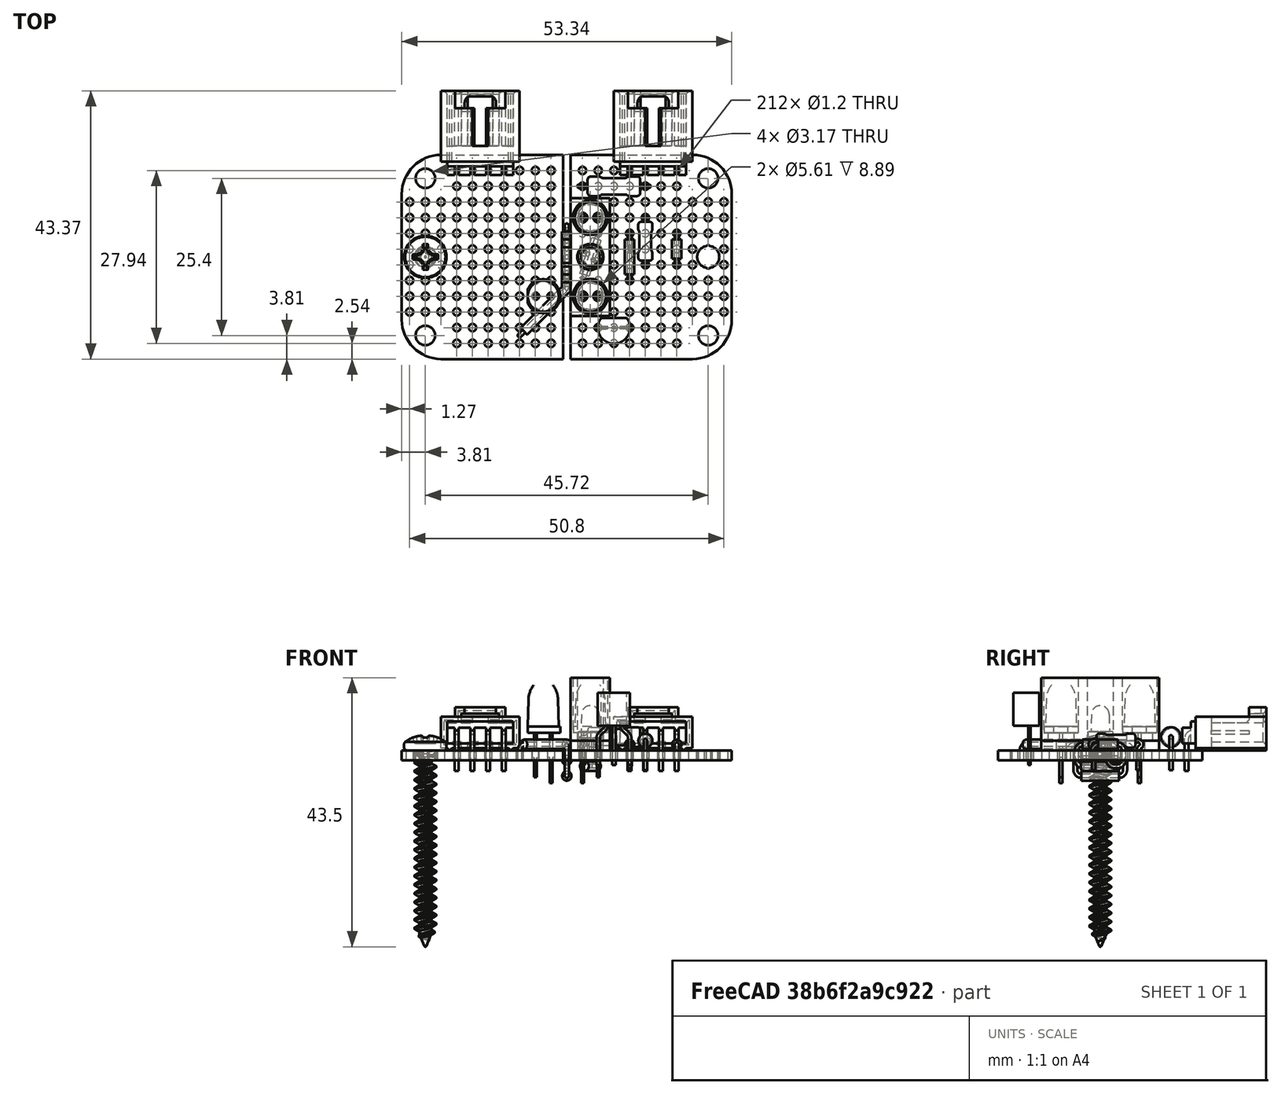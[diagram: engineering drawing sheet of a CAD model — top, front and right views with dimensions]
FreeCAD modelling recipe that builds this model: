
FCSTD DOCUMENT  (FreeCAD 0.21R33771 (Git))
Label: Sensor
License: All rights reserved
LicenseURL: http://en.wikipedia.org/wiki/All_rights_reserved
objects: Sketcher::SketchObject×51, PartDesign::Body×23, TechDraw::DrawViewDimension×21, PartDesign::Pad×16, Part::FeaturePython×14, PartDesign::AdditivePipe×10, PartDesign::LinearPattern×8, PartDesign::Pocket×8, App::Part×7, PartDesign::Revolution×4, PartDesign::MultiTransform×4, TechDraw::DrawProjGroupItem×3, Part::Feature×2, PartDesign::Mirrored×2, TechDraw::DrawSVGTemplate×2, TechDraw::DrawProjGroup×2, TechDraw::DrawPage×2, TechDraw::DrawViewSection×1, PartDesign::SubShapeBinder×1
note: 220 computed .brp shape members not serialized (recipe doc carries the construction recipe); baked Part::Feature solids carry a one-line shape summary decoded from their .brp

FEATURE [Part::Feature] Part__Feature  label="705530003"
  Placement = pos=(-13.97,-21.1455,4.5085) rot=(1,0,0;1.5708rad)
  shape: bbox 12.7 x 13.59 x 10.29 mm, 137 faces (baked)
FEATURE [Part::FeaturePython] Clone  label="705530003-001"  # Draft clone (typed FeaturePython)
  AttacherType = Attacher::AttachEngine3D
  Fuse = false
  Objects = -> [Part__Feature]
  Placement = pos=(-13.97,21.1455,4.5085) rot=(0,0.707107,0.707107;3.14159rad)
  Scale = (1,1,1)
FEATURE [Sketcher::SketchObject] Sketch
  FullyConstrained = true
  MapMode = 5
  Support = -> [XY_Plane]
  sketch-geometry (3):
    g0: ArcOfCircle CenterX=0 CenterY=0 CenterZ=0 NormalX=0 NormalY=0 NormalZ=1 AngleXU=0 Radius=2 StartAngle=5.43512 EndAngle=10.2728
    g1: LineSegment StartX=-1.32288 StartY=-1.5 StartZ=0 EndX=1.32288 EndY=-1.5 EndZ=0
    g2: Circle CenterX=0 CenterY=0 CenterZ=0 NormalX=0 NormalY=0 NormalZ=1 AngleXU=0 Radius=1.5
  constraints (8):
    c: Coincident(g0,g-1)
    c: Coincident(g1,g0)
    c: Coincident(g1,g0)
    c: Horizontal(g1)
    c: Diameter(g0) = 4
    c: Coincident(g2,g0)
    c: Diameter(g2) = 3
    c: Tangent(g1,g2)
FEATURE [PartDesign::Pad] Pad
  Direction = (0,0,1)
  Length = 1
  Length2 = 10
  Profile = -> Sketch
  ReferenceAxis = -> Sketch [N_Axis]
  Type = 0
FEATURE [Sketcher::SketchObject] Sketch001
  ExternalGeometry = -> [Sketch]
  FullyConstrained = true
  MapMode = 5
  Placement = pos=(0,0,0) rot=(0.57735,0.57735,0.57735;2.0944rad)
  Support = -> [YZ_Plane]
  sketch-geometry (4):
    g0: LineSegment StartX=0 StartY=5.2 StartZ=0 EndX=0 EndY=1 EndZ=0
    g1: LineSegment StartX=0 StartY=1 StartZ=0 EndX=-1.5 EndY=1 EndZ=0
    g2: LineSegment StartX=-1.5 StartY=1 StartZ=0 EndX=-1.42641 EndY=3.81046 EndZ=0
    g3: ArcOfCircle CenterX=0 CenterY=3.77311 CenterZ=0 NormalX=0 NormalY=0 NormalZ=1 AngleXU=0 Radius=1.42689 StartAngle=1.5708 EndAngle=3.11541
  constraints (12):
    c: PointOnObject(g0,g-2)
    c: DistanceY(g-1,g0) = 5.2
    c: Vertical(g0)
    c: Coincident(g0,g1)
    c: Horizontal(g1)
    c: Coincident(g1,g2)
    c: Tangent(g2,g3) = 1.5708
    c: Angle(g2) = 1.54462
    c: Vertical(g1,g-3)
    c: DistanceY(g-1,g1) = 1
    c: Coincident(g3,g0)
    c: PointOnObject(g3,g-2)
FEATURE [PartDesign::Revolution] Revolution
  Angle = 360
  Axis = (-2e-16,3e-16,1)
  Base = (0,0,0)
  BaseFeature = -> Pad
  Profile = -> Sketch001
  ReferenceAxis = -> Sketch001 [V_Axis]
FEATURE [Sketcher::SketchObject] Sketch002
  FullyConstrained = true
  MapMode = 5
  Placement = pos=(0,0,0) rot=(0.57735,0.57735,0.57735;2.0944rad)
  Support = -> [YZ_Plane]
  sketch-geometry (33):
    g0: LineSegment StartX=-0.325 StartY=0 StartZ=0 EndX=-1.52 EndY=0 EndZ=0
    g1: LineSegment StartX=0.325 StartY=0 StartZ=0 EndX=1.52 EndY=0 EndZ=0
    g2: LineSegment StartX=-2.04605 StartY=-1.71307 StartZ=0 EndX=-2.04605 EndY=-3.175 EndZ=0
    g3: LineSegment StartX=-2.04605 StartY=-3.175 StartZ=0 EndX=-1.54605 EndY=-3.175 EndZ=0
    g4: LineSegment StartX=-1.54605 StartY=-3.175 StartZ=0 EndX=-1.54605 EndY=-1.71307 EndZ=0
    g5: LineSegment StartX=2.04605 StartY=-1.71307 StartZ=0 EndX=2.04605 EndY=-3.175 EndZ=0
    g6: LineSegment StartX=2.04605 StartY=-3.175 StartZ=0 EndX=1.54605 EndY=-3.175 EndZ=0
    g7: LineSegment StartX=1.54605 StartY=-3.175 StartZ=0 EndX=1.54605 EndY=-1.71307 EndZ=0
    g8: LineSegment StartX=-2.04605 StartY=-3.175 StartZ=0 EndX=-0.25 EndY=-1.37895 EndZ=0
    g9: LineSegment StartX=-0.25 StartY=-1.37895 StartZ=0 EndX=1.54605 EndY=-3.175 EndZ=0
    g10: LineSegment StartX=-0.325 StartY=0 StartZ=0 EndX=-0.325 EndY=-0.4 EndZ=0
    g11: LineSegment StartX=-0.325 StartY=-0.4 StartZ=0 EndX=-1.02 EndY=-0.4 EndZ=0
    g12: LineSegment StartX=0.325 StartY=0 StartZ=0 EndX=0.325 EndY=-0.4 EndZ=0
    g13: LineSegment StartX=0.325 StartY=-0.4 StartZ=0 EndX=1.02 EndY=-0.4 EndZ=0
    g14: LineSegment StartX=-1.52 StartY=0 StartZ=0 EndX=-1.52 EndY=-0.4 EndZ=0
    g15: LineSegment StartX=1.52 StartY=0 StartZ=0 EndX=1.52 EndY=-0.4 EndZ=0
    g16: ArcOfCircle CenterX=-2.02 CenterY=-0.4 CenterZ=0 NormalX=0 NormalY=0 NormalZ=1 AngleXU=0 Radius=0.5 StartAngle=5.75959 EndAngle=6.28319
    g17: LineSegment StartX=-1.58699 StartY=-0.65 StartZ=0 EndX=-1.91208 EndY=-1.21307 EndZ=0
    g18: LineSegment StartX=-1.02 StartY=-0.4 StartZ=0 EndX=-1.52 EndY=-0.4 EndZ=0
    g19: LineSegment StartX=-1.52 StartY=-0.4 StartZ=0 EndX=-2.02 EndY=-0.4 EndZ=0
    g20: ArcOfCircle CenterX=-2.02 CenterY=-0.4 CenterZ=0 NormalX=0 NormalY=0 NormalZ=1 AngleXU=0 Radius=1 StartAngle=5.75959 EndAngle=6.28319
    g21: LineSegment StartX=-1.91208 StartY=-1.21307 StartZ=0 EndX=-2.23717 EndY=-0.65 EndZ=0
    g22: LineSegment StartX=-2.23717 StartY=-0.65 StartZ=0 EndX=-1.58699 EndY=-0.65 EndZ=0
    g23: ArcOfCircle CenterX=2.02 CenterY=-0.4 CenterZ=0 NormalX=0 NormalY=0 NormalZ=1 AngleXU=0 Radius=0.5 StartAngle=3.14159 EndAngle=3.66519
    g24: LineSegment StartX=1.58699 StartY=-0.65 StartZ=0 EndX=1.91208 EndY=-1.21307 EndZ=0
    g25: ArcOfCircle CenterX=2.02 CenterY=-0.4 CenterZ=0 NormalX=0 NormalY=0 NormalZ=1 AngleXU=0 Radius=1 StartAngle=3.14159 EndAngle=3.66519
    g26: LineSegment StartX=-1.15397 StartY=-0.9 StartZ=0 EndX=-1.47906 EndY=-1.46307 EndZ=0
    g27: ArcOfCircle CenterX=-1.04605 CenterY=-1.71307 CenterZ=0 NormalX=0 NormalY=0 NormalZ=1 AngleXU=0 Radius=0.5 StartAngle=2.61799 EndAngle=3.14159
    g28: ArcOfCircle CenterX=-1.04605 CenterY=-1.71307 CenterZ=0 NormalX=0 NormalY=0 NormalZ=1 AngleXU=0 Radius=1 StartAngle=2.61799 EndAngle=3.14159
    g29: LineSegment StartX=1.15397 StartY=-0.9 StartZ=0 EndX=1.47906 EndY=-1.46307 EndZ=0
    g30: ArcOfCircle CenterX=1.04605 CenterY=-1.71307 CenterZ=0 NormalX=0 NormalY=0 NormalZ=1 AngleXU=0 Radius=0.5 StartAngle=2e-16 EndAngle=0.523599
    g31: ArcOfCircle CenterX=1.04605 CenterY=-1.71307 CenterZ=0 NormalX=0 NormalY=0 NormalZ=1 AngleXU=0 Radius=1 StartAngle=0 EndAngle=0.523599
    g32: LineSegment StartX=-1.52 StartY=-0.65 StartZ=0 EndX=1.02 EndY=-0.65 EndZ=0
  constraints (85):
    c: PointOnObject(g0,g-1)
    c: Horizontal(g0)
    c: Horizontal(g1)
    c: Symmetric(g0,g1,g-2)
    c: Equal(g0,g1)
    c: Coincident(g2,g3)
    c: Horizontal(g3)
    c: Coincident(g3,g4)
    c: Vertical(g4)
    c: Vertical(g2)
    c: Coincident(g5,g6)
    c: Horizontal(g6)
    c: Coincident(g6,g7)
    c: Vertical(g7)
    c: Vertical(g5)
    c: Equal(g4,g7)
    c: Coincident(g2,g8)
    c: Coincident(g8,g9)
    c: Coincident(g9,g6)
    c: Perpendicular(g9,g8)
    c: DistanceX(g0,g1) = 0.65
    c: Coincident(g0,g10)
    c: Vertical(g10)
    c: Coincident(g10,g11)
    c: Horizontal(g11)
    c: Coincident(g1,g12)
    c: Vertical(g12)
    c: Coincident(g12,g13)
    c: Horizontal(g13)
    c: DistanceY(g10,g10) = 0.4
    c: Equal(g10,g12)
    c: Coincident(g14,g0)
    c: Vertical(g14)
    c: Coincident(g15,g1)
    c: Vertical(g15)
    c: DistanceX(g0,g11) = 0.5
    c: Equal(g11,g13)
    c: Tangent(g14,g16) = 1.5708
    c: Tangent(g16,g17) = 1.5708
    c: Coincident(g18,g11)
    c: Coincident(g18,g14)
    c: Horizontal(g18)
    c: Coincident(g19,g14)
    c: Coincident(g19,g16)
    c: Equal(g18,g19)
    c: Coincident(g20,g16)
    c: Coincident(g20,g11)
    c: Coincident(g17,g21)
    c: Coincident(g21,g22)
    c: Coincident(g22,g16)
    c: Horizontal(g22)
    c: Equal(g22,g17)
    c: Equal(g22,g21)
    c: DistanceX(g0,g13) = 2.54
    c: Tangent(g15,g23) = -1.5708
    c: Tangent(g23,g24) = -1.5708
    c: Coincident(g25,g23)
    c: Coincident(g25,g13)
    c: Equal(g23,g16)
    c: PointOnObject(g23,g13)
    c: Parallel(g24,g21)
    c: Tangent(g20,g26) = 1.5708
    c: Tangent(g26,g27) = -1.5708
    c: Tangent(g17,g28) = -1.5708
    c: Tangent(g25,g29) = -1.5708
    c: Tangent(g29,g30) = 1.5708
    c: Tangent(g24,g31) = 1.5708
    c: Parallel(g29,g21)
    c: Parallel(g17,g26)
    c: Equal(g16,g27)
    c: Equal(g16,g30)
    c: Coincident(g27,g28)
    c: Coincident(g30,g31)
    c: Tangent(g4,g27) = 1.5708
    c: Tangent(g2,g28) = -1.5708
    c: Tangent(g30,g7) = -1.5708
    c: Tangent(g5,g31) = 1.5708
    c: Horizontal(g32)
    c: PointOnObject(g32,g14)
    c: PointOnObject(g21,g32)
    c: Vertical(g32,g13)
    c: Equal(g32,g8)
    c: Equal(g32,g9)
    c: Horizontal(g2,g6)
    c: DistanceY(g2,g-1) = 3.175
FEATURE [PartDesign::Pad] Pad001
  BaseFeature = -> Revolution
  Direction = (1,-2e-16,3e-16)
  Length = 0.5
  Length2 = 10
  Midplane = true
  Profile = -> Sketch002
  ReferenceAxis = -> Sketch002 [N_Axis]
  Type = 0
FEATURE [PartDesign::Body] Body  label="ALS-PT204-6C/L177"
  Group = -> [Sketch,Pad,Sketch001,Revolution,Sketch002,Pad001]
  Origin = -> Origin
  Placement = pos=(-3.81,0,3.575) rot=(0,0,1;0.785398rad)
  Tip = -> Pad001
FEATURE [Sketcher::SketchObject] Sketch003
  FullyConstrained = true
  MapMode = 5
  Support = -> [XY_Plane001]
  sketch-geometry (3):
    g0: ArcOfCircle CenterX=0 CenterY=0 CenterZ=0 NormalX=0 NormalY=0 NormalZ=1 AngleXU=0 Radius=2.75 StartAngle=5.14209 EndAngle=10.5659
    g1: LineSegment StartX=-1.14564 StartY=-2.5 StartZ=0 EndX=1.14564 EndY=-2.5 EndZ=0
    g2: Circle CenterX=0 CenterY=0 CenterZ=0 NormalX=0 NormalY=0 NormalZ=1 AngleXU=0 Radius=2.5
  constraints (8):
    c: Coincident(g0,g-1)
    c: Coincident(g1,g0)
    c: Coincident(g1,g0)
    c: Horizontal(g1)
    c: Diameter(g0) = 5.5
    c: Coincident(g2,g0)
    c: Diameter(g2) = 5
    c: Tangent(g1,g2)
FEATURE [PartDesign::Pad] Pad002
  Direction = (0,0,1)
  Length = 1
  Length2 = 10
  Profile = -> Sketch003
  ReferenceAxis = -> Sketch003 [N_Axis]
  Type = 0
FEATURE [Sketcher::SketchObject] Sketch004
  ExternalGeometry = -> [Sketch003]
  FullyConstrained = true
  MapMode = 5
  Placement = pos=(0,0,0) rot=(0.57735,0.57735,0.57735;2.0944rad)
  Support = -> [YZ_Plane001]
  sketch-geometry (7):
    g0: ArcOfParabola CenterX=0 CenterY=8.7 CenterZ=0 NormalX=0 NormalY=0 NormalZ=1 Focal=0.600182 AngleXU=-1.5708 StartAngle=-1.54943 EndAngle=0
    g1: GeomPoint X=0 Y=8.09982 Z=0
    g2: LineSegment StartX=0 StartY=8.7 StartZ=0 EndX=0 EndY=8.09982 EndZ=0
    g3: LineSegment StartX=0 StartY=8.7 StartZ=0 EndX=0 EndY=1 EndZ=0
    g4: LineSegment StartX=0 StartY=1 StartZ=0 EndX=-2.5 EndY=1 EndZ=0
    g5: LineSegment StartX=-2.5 StartY=1 StartZ=0 EndX=-2.38596 EndY=5.35499 EndZ=0
    g6: ArcOfCircle CenterX=1.61267 CenterY=5.25028 CenterZ=0 NormalX=0 NormalY=0 NormalZ=1 AngleXU=0 Radius=4 StartAngle=2.48246 EndAngle=3.11541
  constraints (18):
    c: InternalAlignment(g1,g0)
    c: InternalAlignment(g2,g0)
    c: PointOnObject(g1,g-2)
    c: PointOnObject(g0,g-2)
    c: Vertical(g2)
    c: DistanceY(g-1,g0) = 8.7
    c: DistanceY(g0,g0) = 1
    c: Vertical(g3)
    c: Coincident(g3,g4)
    c: Horizontal(g4)
    c: Coincident(g4,g5)
    c: Tangent(g5,g6) = 1.5708
    c: Coincident(g3,g0)
    c: Angle(g5) = 1.54462
    c: Vertical(g4,g-3)
    c: Tangent(g6,g0) = 1.5708
    c: DistanceY(g-1,g4) = 1
    c: Radius(g6) = 4
FEATURE [PartDesign::Revolution] Revolution001
  Angle = 360
  Axis = (-2e-16,3e-16,1)
  Base = (0,0,0)
  BaseFeature = -> Pad002
  Profile = -> Sketch004
  ReferenceAxis = -> Sketch004 [V_Axis]
FEATURE [Sketcher::SketchObject] Sketch005
  FullyConstrained = true
  MapMode = 5
  Placement = pos=(0,0,0) rot=(0.57735,0.57735,0.57735;2.0944rad)
  Support = -> [YZ_Plane001]
  sketch-geometry (24):
    g0: LineSegment StartX=-1.52 StartY=0 StartZ=0 EndX=-1.52 EndY=-2.9 EndZ=0
    g1: LineSegment StartX=-1.52 StartY=-2.9 StartZ=0 EndX=-1.82 EndY=-2.9 EndZ=0
    g2: LineSegment StartX=-1.82 StartY=-2.9 StartZ=0 EndX=-1.82 EndY=-4 EndZ=0
    g3: LineSegment StartX=-1.82 StartY=-4 StartZ=0 EndX=-1.52 EndY=-4 EndZ=0
    g4: LineSegment StartX=-1.52 StartY=-4 StartZ=0 EndX=-1.52 EndY=-7.175 EndZ=0
    g5: LineSegment StartX=-1.52 StartY=-7.175 StartZ=0 EndX=-1.02 EndY=-7.175 EndZ=0
    g6: LineSegment StartX=-1.02 StartY=-7.175 StartZ=0 EndX=-1.02 EndY=-4 EndZ=0
    g7: LineSegment StartX=-1.02 StartY=-4 StartZ=0 EndX=-0.72 EndY=-4 EndZ=0
    g8: LineSegment StartX=-0.72 StartY=-4 StartZ=0 EndX=-0.72 EndY=-2.9 EndZ=0
    g9: LineSegment StartX=-0.72 StartY=-2.9 StartZ=0 EndX=-1.02 EndY=-2.9 EndZ=0
    g10: LineSegment StartX=-1.02 StartY=-2.9 StartZ=0 EndX=-1.02 EndY=0 EndZ=0
    g11: LineSegment StartX=-1.02 StartY=0 StartZ=0 EndX=-1.52 EndY=0 EndZ=0
    g12: LineSegment StartX=1.02 StartY=0 StartZ=0 EndX=1.52 EndY=0 EndZ=0
    g13: LineSegment StartX=1.52 StartY=0 StartZ=0 EndX=1.52 EndY=-2.9 EndZ=0
    g14: LineSegment StartX=1.52 StartY=-2.9 StartZ=0 EndX=1.82 EndY=-2.9 EndZ=0
    g15: LineSegment StartX=1.82 StartY=-2.9 StartZ=0 EndX=1.82 EndY=-4 EndZ=0
    g16: LineSegment StartX=1.82 StartY=-4 StartZ=0 EndX=1.52 EndY=-4 EndZ=0
    g17: LineSegment StartX=1.52 StartY=-4 StartZ=0 EndX=1.52 EndY=-8.175 EndZ=0
    g18: LineSegment StartX=1.52 StartY=-8.175 StartZ=0 EndX=1.02 EndY=-8.175 EndZ=0
    g19: LineSegment StartX=1.02 StartY=-8.175 StartZ=0 EndX=1.02 EndY=-4 EndZ=0
    g20: LineSegment StartX=1.02 StartY=-4 StartZ=0 EndX=0.72 EndY=-4 EndZ=0
    g21: LineSegment StartX=0.72 StartY=-4 StartZ=0 EndX=0.72 EndY=-2.9 EndZ=0
    g22: LineSegment StartX=0.72 StartY=-2.9 StartZ=0 EndX=1.02 EndY=-2.9 EndZ=0
    g23: LineSegment StartX=1.02 StartY=-2.9 StartZ=0 EndX=1.02 EndY=0 EndZ=0
  constraints (71):
    c: PointOnObject(g0,g-1)
    c: Vertical(g0)
    c: Coincident(g0,g1)
    c: Horizontal(g1)
    c: Coincident(g1,g2)
    c: Vertical(g2)
    c: Coincident(g2,g3)
    c: Horizontal(g3)
    c: Coincident(g3,g4)
    c: Vertical(g4)
    c: Coincident(g4,g5)
    c: Horizontal(g5)
    c: Coincident(g5,g6)
    c: Vertical(g6)
    c: Coincident(g6,g7)
    c: Horizontal(g7)
    c: Coincident(g7,g8)
    c: Vertical(g8)
    c: Coincident(g8,g9)
    c: Horizontal(g9)
    c: Coincident(g9,g10)
    c: Vertical(g10)
    c: Coincident(g10,g11)
    c: Coincident(g11,g0)
    c: Horizontal(g11)
    c: DistanceX(g11,g11) = 0.5
    c: Equal(g1,g9)
    c: Equal(g0,g10)
    c: Equal(g2,g8)
    c: DistanceY(g7,g-1) = 4
    c: DistanceY(g8,g8) = 1.1
    c: DistanceX(g1,g8) = 1.1
    c: Horizontal(g12)
    c: Coincident(g12,g13)
    c: Vertical(g13)
    c: Coincident(g13,g14)
    c: Horizontal(g14)
    c: Coincident(g14,g15)
    c: Vertical(g15)
    c: Coincident(g15,g16)
    c: Horizontal(g16)
    c: Coincident(g16,g17)
    c: Vertical(g17)
    c: Coincident(g17,g18)
    c: Horizontal(g18)
    c: Coincident(g18,g19)
    c: Vertical(g19)
    c: Coincident(g19,g20)
    c: Horizontal(g20)
    c: Coincident(g20,g21)
    c: Vertical(g21)
    c: Coincident(g21,g22)
    c: Horizontal(g22)
    c: Coincident(g22,g23)
    c: Coincident(g23,g12)
    c: Vertical(g23)
    c: Symmetric(g10,g12,g-2)
    c: DistanceX(g0,g12) = 2.54
    c: Equal(g9,g7)
    c: Equal(g9,g3)
    c: Equal(g11,g12)
    c: Equal(g9,g22)
    c: Equal(g9,g14)
    c: Equal(g20,g9)
    c: Equal(g16,g9)
    c: Equal(g10,g23)
    c: Equal(g10,g13)
    c: Equal(g8,g21)
    c: Equal(g8,g15)
    c: DistanceY(g18,g5) = 1
    c: DistanceY(g4,g2) = 3.175
FEATURE [PartDesign::Pad] Pad003
  BaseFeature = -> Revolution001
  Direction = (1,-2e-16,3e-16)
  Length = 0.5
  Length2 = 10
  Midplane = true
  Profile = -> Sketch005
  ReferenceAxis = -> Sketch005 [N_Axis]
  Type = 0
FEATURE [PartDesign::Body] Body001  label="VLCS5830"
  Group = -> [Sketch003,Pad002,Sketch004,Revolution001,Sketch005,Pad003]
  Origin = -> Origin001
  Placement = pos=(-3.81,6.35,4.445) rot=(0,0,-1;1.5708rad)
  Tip = -> Pad003
FEATURE [Sketcher::SketchObject] Sketch006
  FullyConstrained = true
  MapMode = 5
  Support = -> [XY_Plane002]
  sketch-geometry (3):
    g0: ArcOfCircle CenterX=0 CenterY=0 CenterZ=0 NormalX=0 NormalY=0 NormalZ=1 AngleXU=0 Radius=2.6035 StartAngle=5.62743 EndAngle=10.0805
    g1: LineSegment StartX=-2.06351 StartY=-1.5875 StartZ=0 EndX=2.06351 EndY=-1.5875 EndZ=0
    g2: GeomPoint X=0 Y=2.6035 Z=0
  constraints (8):
    c: Coincident(g0,g-1)
    c: Coincident(g1,g0)
    c: Coincident(g1,g0)
    c: Horizontal(g1)
    c: Diameter(g0) = 5.207
    c: PointOnObject(g2,g0)
    c: PointOnObject(g2,g-2)
    c: DistanceY(g0,g2) = 4.191
FEATURE [PartDesign::Pad] Pad004
  Direction = (0,0,1)
  Length = 5.334
  Length2 = 10
  Profile = -> Sketch006
  ReferenceAxis = -> Sketch006 [N_Axis]
  Type = 0
FEATURE [Sketcher::SketchObject] Sketch007
  FullyConstrained = true
  MapMode = 5
  Placement = pos=(0,0,0) rot=(1,0,0;1.5708rad)
  Support = -> [XZ_Plane002]
  sketch-geometry (29):
    g0: LineSegment StartX=-0.2794 StartY=0 StartZ=0 EndX=0.2794 EndY=0 EndZ=0
    g1: LineSegment StartX=0.2794 StartY=0 StartZ=0 EndX=0.2794 EndY=-6.35 EndZ=0
    g2: LineSegment StartX=0.2794 StartY=-6.35 StartZ=0 EndX=-0.2794 EndY=-6.35 EndZ=0
    g3: LineSegment StartX=-0.2794 StartY=-6.35 StartZ=0 EndX=-0.2794 EndY=0 EndZ=0
    g4: LineSegment StartX=-2.2606 StartY=-6.35 StartZ=0 EndX=-2.2606 EndY=-1.96439 EndZ=0
    g5: ArcOfCircle CenterX=-1.7018 CenterY=-1.96439 CenterZ=0 NormalX=0 NormalY=0 NormalZ=1 AngleXU=0 Radius=0.5588 StartAngle=2.35619 EndAngle=3.14159
    g6: LineSegment StartX=-2.09693 StartY=-1.56926 StartZ=0 EndX=-1.31794 EndY=-0.790263 EndZ=0
    g7: LineSegment StartX=-2.2606 StartY=-6.35 StartZ=0 EndX=-2.8194 EndY=-6.35 EndZ=0
    g8: LineSegment StartX=-2.8194 StartY=-6.35 StartZ=0 EndX=-2.8194 EndY=-1.96439 EndZ=0
    g9: ArcOfCircle CenterX=-1.7018 CenterY=-1.96439 CenterZ=0 NormalX=0 NormalY=0 NormalZ=1 AngleXU=0 Radius=1.1176 StartAngle=2.35619 EndAngle=3.14159
    g10: LineSegment StartX=-2.49206 StartY=-1.17413 StartZ=0 EndX=-1.71307 EndY=-0.395131 EndZ=0
    g11: ArcOfCircle CenterX=-2.1082 CenterY=0 CenterZ=0 NormalX=0 NormalY=0 NormalZ=1 AngleXU=0 Radius=0.5588 StartAngle=5.49779 EndAngle=6.28319
    g12: LineSegment StartX=-1.5494 StartY=0 StartZ=0 EndX=-0.9906 EndY=0 EndZ=0
    g13: ArcOfCircle CenterX=-2.1082 CenterY=0 CenterZ=0 NormalX=0 NormalY=0 NormalZ=1 AngleXU=0 Radius=1.1176 StartAngle=5.49779 EndAngle=6.28319
    g14: LineSegment StartX=-0.9906 StartY=0 StartZ=0 EndX=-0.2794 EndY=0 EndZ=0
    g15: LineSegment StartX=-2.1082 StartY=0 StartZ=0 EndX=-1.5494 EndY=0 EndZ=0
    g16: LineSegment StartX=-2.49206 StartY=-1.17413 StartZ=0 EndX=-2.49206 EndY=-0.395131 EndZ=0
    g17: LineSegment StartX=-2.49206 StartY=-0.395131 StartZ=0 EndX=-1.71307 EndY=-0.395131 EndZ=0
    g18: LineSegment StartX=0.9906 StartY=0 StartZ=0 EndX=1.5494 EndY=0 EndZ=0
    g19: ArcOfCircle CenterX=2.1082 CenterY=-1e-16 CenterZ=0 NormalX=0 NormalY=0 NormalZ=1 AngleXU=0 Radius=0.5588 StartAngle=3.14159 EndAngle=3.92699
    g20: LineSegment StartX=1.71307 StartY=-0.395131 StartZ=0 EndX=2.49206 EndY=-1.17413 EndZ=0
    g21: ArcOfCircle CenterX=1.7018 CenterY=-1.96439 CenterZ=0 NormalX=0 NormalY=0 NormalZ=1 AngleXU=0 Radius=1.1176 StartAngle=1e-16 EndAngle=0.785398
    g22: LineSegment StartX=2.8194 StartY=-1.96439 StartZ=0 EndX=2.8194 EndY=-6.35 EndZ=0
    g23: LineSegment StartX=2.8194 StartY=-6.35 StartZ=0 EndX=2.2606 EndY=-6.35 EndZ=0
    g24: LineSegment StartX=2.2606 StartY=-6.35 StartZ=0 EndX=2.2606 EndY=-1.96439 EndZ=0
    g25: ArcOfCircle CenterX=1.7018 CenterY=-1.96439 CenterZ=0 NormalX=0 NormalY=0 NormalZ=1 AngleXU=0 Radius=0.5588 StartAngle=0 EndAngle=0.785398
    g26: LineSegment StartX=2.09693 StartY=-1.56926 StartZ=0 EndX=1.31794 EndY=-0.790263 EndZ=0
    g27: ArcOfCircle CenterX=2.1082 CenterY=-1e-16 CenterZ=0 NormalX=0 NormalY=0 NormalZ=1 AngleXU=0 Radius=1.1176 StartAngle=3.14159 EndAngle=3.92699
    g28: LineSegment StartX=0.2794 StartY=0 StartZ=0 EndX=0.9906 EndY=0 EndZ=0
  constraints (73):
    c: Coincident(g0,g1)
    c: Coincident(g1,g2)
    c: Coincident(g2,g3)
    c: Coincident(g3,g0)
    c: Horizontal(g0)
    c: Horizontal(g2)
    c: Vertical(g1)
    c: Vertical(g3)
    c: Symmetric(g0,g0,g-1)
    c: DistanceX(g0,g0) = 0.5588
    c: DistanceY(g1,g1) = 6.35
    c: Vertical(g4)
    c: Tangent(g4,g5) = 1.5708
    c: Tangent(g5,g6) = 1.5708
    c: Coincident(g4,g7)
    c: Horizontal(g7)
    c: Coincident(g7,g8)
    c: Vertical(g8)
    c: Tangent(g8,g9) = 1.5708
    c: Tangent(g9,g10) = 1.5708
    c: Tangent(g10,g11) = -1.5708
    c: Horizontal(g12)
    c: PointOnObject(g11,g12)
    c: Coincident(g9,g5)
    c: Coincident(g13,g11)
    c: Coincident(g13,g12)
    c: Tangent(g13,g6) = -1.5708
    c: Equal(g11,g5)
    c: Equal(g9,g13)
    c: Equal(g0,g12)
    c: Coincident(g11,g12)
    c: Coincident(g14,g12)
    c: Coincident(g14,g0)
    c: Horizontal(g14)
    c: Coincident(g15,g11)
    c: Coincident(g15,g11)
    c: Equal(g15,g0)
    c: Coincident(g16,g9)
    c: Vertical(g16)
    c: Coincident(g17,g16)
    c: Coincident(g17,g10)
    c: Horizontal(g17)
    c: Equal(g16,g17)
    c: DistanceX(g11,g0) = 1.27
    c: PointOnObject(g4,g2)
    c: DistanceX(g7,g2) = 2.54
    c: Horizontal(g18)
    c: Perpendicular(g18,g19) = 4.71239
    c: Tangent(g19,g20) = -1.5708
    c: Tangent(g20,g21) = 1.5708
    c: Tangent(g21,g22) = 1.5708
    c: Coincident(g22,g23)
    c: Horizontal(g23)
    c: Coincident(g23,g24)
    c: Vertical(g24)
    c: Tangent(g24,g25) = -1.5708
    c: Tangent(g25,g26) = -1.5708
    c: Tangent(g26,g27) = 1.5708
    c: Coincident(g27,g18)
    c: Coincident(g28,g0)
    c: Coincident(g28,g18)
    c: Horizontal(g28)
    c: Equal(g28,g14)
    c: Coincident(g27,g19)
    c: Coincident(g25,g21)
    c: Vertical(g22)
    c: Equal(g11,g19)
    c: Equal(g25,g11)
    c: Equal(g13,g27)
    c: Equal(g13,g21)
    c: Perpendicular(g10,g20)
    c: PointOnObject(g1,g23)
    c: Equal(g10,g20)
FEATURE [PartDesign::Pad] Pad005
  BaseFeature = -> Pad004
  Direction = (0,-1,-2e-16)
  Length = 0.381
  Length2 = 10
  Midplane = true
  Profile = -> Sketch007
  ReferenceAxis = -> Sketch007 [N_Axis]
  Type = 0
FEATURE [PartDesign::Body] Body002  label="TO-92"
  Group = -> [Sketch006,Pad004,Sketch007,Pad005]
  Origin = -> Origin002
  Placement = pos=(-7.62,11.43,5.58749) rot=(0,0,1;0rad)
  Tip = -> Pad005
FEATURE [Sketcher::SketchObject] Sketch008
  FullyConstrained = true
  MapMode = 5
  Support = -> [XY_Plane003]
  sketch-geometry (12):
    g0: LineSegment StartX=-20.32 StartY=16.51 StartZ=0 EndX=20.32 EndY=16.51 EndZ=0
    g1: LineSegment StartX=26.67 StartY=10.16 StartZ=0 EndX=26.67 EndY=-10.16 EndZ=0
    g2: LineSegment StartX=20.32 StartY=-16.51 StartZ=0 EndX=-20.32 EndY=-16.51 EndZ=0
    g3: LineSegment StartX=-26.67 StartY=-10.16 StartZ=0 EndX=-26.67 EndY=10.16 EndZ=0
    g4: ArcOfCircle CenterX=-20.32 CenterY=10.16 CenterZ=0 NormalX=0 NormalY=0 NormalZ=1 AngleXU=0 Radius=6.35 StartAngle=1.5708 EndAngle=3.14159
    g5: ArcOfCircle CenterX=-20.32 CenterY=-10.16 CenterZ=0 NormalX=0 NormalY=0 NormalZ=1 AngleXU=0 Radius=6.35 StartAngle=3.14159 EndAngle=4.71239
    g6: ArcOfCircle CenterX=20.32 CenterY=-10.16 CenterZ=0 NormalX=0 NormalY=0 NormalZ=1 AngleXU=0 Radius=6.35 StartAngle=4.71239 EndAngle=6.28319
    g7: ArcOfCircle CenterX=20.32 CenterY=10.16 CenterZ=0 NormalX=0 NormalY=0 NormalZ=1 AngleXU=0 Radius=6.35 StartAngle=0 EndAngle=1.5708
    g8: Circle CenterX=-22.86 CenterY=-12.7 CenterZ=0 NormalX=0 NormalY=0 NormalZ=1 AngleXU=0 Radius=1.5875
    g9: Circle CenterX=-22.86 CenterY=12.7 CenterZ=0 NormalX=0 NormalY=0 NormalZ=1 AngleXU=0 Radius=1.5875
    g10: Circle CenterX=22.86 CenterY=12.7 CenterZ=0 NormalX=0 NormalY=0 NormalZ=1 AngleXU=0 Radius=1.5875
    g11: Circle CenterX=22.86 CenterY=-12.7 CenterZ=0 NormalX=0 NormalY=0 NormalZ=1 AngleXU=0 Radius=1.5875
  constraints (30):
    c: Horizontal(g0)
    c: Horizontal(g2)
    c: Vertical(g1)
    c: Vertical(g3)
    c: Tangent(g0,g4) = 1.5708
    c: Tangent(g3,g4) = 1.5708
    c: Tangent(g3,g5) = 1.5708
    c: Tangent(g2,g5) = 1.5708
    c: Tangent(g2,g6) = 1.5708
    c: Tangent(g1,g6) = 1.5708
    c: Tangent(g1,g7) = 1.5708
    c: Tangent(g0,g7) = 1.5708
    c: Equal(g4,g5)
    c: Equal(g4,g7)
    c: Equal(g6,g4)
    c: Symmetric(g5,g7,g-1)
    c: DistanceX(g3,g1) = 53.34
    c: DistanceY(g2,g0) = 33.02
    c: Radius(g4) = 6.35
    c: Equal(g8,g9)
    c: Equal(g8,g10)
    c: Equal(g11,g8)
    c: Symmetric(g8,g10,g-1)
    c: Vertical(g9,g8)
    c: Horizontal(g9,g10)
    c: Vertical(g10,g11)
    c: Horizontal(g11,g8)
    c: Diameter(g8) = 3.175
    c: DistanceX(g8,g11) = 45.72
    c: DistanceY(g8,g9) = 25.4
FEATURE [PartDesign::Pad] Pad006
  Direction = (0,0,1)
  Length = 1.5875
  Length2 = 10
  Profile = -> Sketch008
  ReferenceAxis = -> Sketch008 [N_Axis]
  Type = 0
FEATURE [Sketcher::SketchObject] Sketch009
  FullyConstrained = true
  MapMode = 5
  Support = -> [XY_Plane003]
  sketch-geometry (1):
    g0: Circle CenterX=-17.78 CenterY=13.97 CenterZ=0 NormalX=0 NormalY=0 NormalZ=1 AngleXU=0 Radius=0.6
  constraints (3):
    c: Diameter(g0) = 1.2
    c: DistanceX(g0,g-1) = 17.78
    c: DistanceY(g-1,g0) = 13.97
FEATURE [PartDesign::LinearPattern] LinearPattern
  Direction = -> Sketch009 [H_Axis]
  Length = 35.56
  Occurrences = 15
FEATURE [PartDesign::LinearPattern] LinearPattern001
  Direction = -> Sketch009 [V_Axis]
  Length = 27.94
  Occurrences = 12
  Reversed = true
FEATURE [PartDesign::Pocket] Pocket
  BaseFeature = -> Pad006
  Direction = (0,0,-1)
  Length = 5
  Length2 = 5
  Profile = -> Sketch009
  ReferenceAxis = -> Sketch009 [N_Axis]
  Reversed = true
  Type = 1
FEATURE [PartDesign::MultiTransform] MultiTransform
  BaseFeature = -> Pocket
  Originals = -> [Pocket]
  Transformations = -> [LinearPattern,LinearPattern001]
FEATURE [Sketcher::SketchObject] Sketch010
  ExternalGeometry = -> [Sketch009]
  FullyConstrained = true
  MapMode = 5
  Support = -> [XY_Plane003]
  sketch-geometry (1):
    g0: Circle CenterX=-25.4 CenterY=8.89 CenterZ=0 NormalX=0 NormalY=0 NormalZ=1 AngleXU=0 Radius=0.6
  constraints (3):
    c: Equal(g0,g-3)
    c: DistanceX(g0,g-1) = 25.4
    c: DistanceY(g-1,g0) = 8.89
FEATURE [PartDesign::LinearPattern] LinearPattern002
  Direction = -> Sketch010 [H_Axis]
  Length = 5.08
  Occurrences = 3
FEATURE [PartDesign::LinearPattern] LinearPattern003
  Direction = -> Sketch010 [V_Axis]
  Length = 17.78
  Occurrences = 8
  Reversed = true
FEATURE [PartDesign::Mirrored] Mirrored
  MirrorPlane = -> Sketch010 [V_Axis]
FEATURE [PartDesign::Pocket] Pocket001
  BaseFeature = -> MultiTransform
  Direction = (0,0,-1)
  Length = 5
  Length2 = 5
  Profile = -> Sketch010
  ReferenceAxis = -> Sketch010 [N_Axis]
  Reversed = true
  Type = 1
FEATURE [PartDesign::MultiTransform] MultiTransform001
  BaseFeature = -> Pocket001
  Originals = -> [Pocket001]
  Transformations = -> [LinearPattern002,LinearPattern003,Mirrored]
FEATURE [Part::FeaturePython] Clone001  label="VLCS5830-1"  # Draft clone (typed FeaturePython)
  AttacherType = Attacher::AttachEngine3D
  Fuse = false
  Objects = -> [Body001]
  Placement = pos=(-3.81,-6.35,4.445) rot=(0,0,-1;1.5708rad)
  Scale = (1,1,1)
FEATURE [Sketcher::SketchObject] Sketch011
  ExternalGeometry = -> [Sketch008]
  FullyConstrained = true
  MapMode = 5
  Support = -> [XY_Plane003]
  sketch-geometry (5):
    g0: LineSegment StartX=-0.6 StartY=16.51 StartZ=0 EndX=26.67 EndY=16.51 EndZ=0
    g1: LineSegment StartX=26.67 StartY=16.51 StartZ=0 EndX=26.67 EndY=-16.51 EndZ=0
    g2: LineSegment StartX=26.67 StartY=-16.51 StartZ=0 EndX=-0.6 EndY=-16.51 EndZ=0
    g3: LineSegment StartX=-0.6 StartY=-16.51 StartZ=0 EndX=-0.6 EndY=16.51 EndZ=0
    g4: Circle CenterX=-22.86 CenterY=0 CenterZ=0 NormalX=0 NormalY=0 NormalZ=1 AngleXU=0 Radius=1.78435
  constraints (15):
    c: Coincident(g0,g1)
    c: Coincident(g1,g2)
    c: Coincident(g2,g3)
    c: Coincident(g3,g0)
    c: Horizontal(g0)
    c: Horizontal(g2)
    c: Vertical(g1)
    c: Vertical(g3)
    c: PointOnObject(g-4,g2)
    c: PointOnObject(g-4,g1)
    c: PointOnObject(g-3,g0)
    c: DistanceX(g0,g-1) = 0.6
    c: PointOnObject(g4,g-1)
    c: Diameter(g4) = 3.5687
    c: Vertical(g-5,g4)
FEATURE [PartDesign::Pocket] Pocket002
  BaseFeature = -> MultiTransform001
  Direction = (0,0,-1)
  Length = 5
  Length2 = 5
  Profile = -> Sketch011
  ReferenceAxis = -> Sketch011 [N_Axis]
  Reversed = true
  Type = 1
FEATURE [PartDesign::Body] Body003  label="Perma-Proto, Small Mint Tin"
  Group = -> [Sketch008,Pad006,Sketch009,Sketch010,Pocket,MultiTransform,LinearPattern,LinearPattern001,Pocket001,MultiTransform001,LinearPattern002,LinearPattern003,Mirrored,Sketch011,Pocket002]
  Origin = -> Origin003
  Tip = -> Pocket002
FEATURE [Sketcher::SketchObject] Sketch012
  FullyConstrained = true
  MapMode = 5
  Placement = pos=(0,0,0) rot=(1,0,0;1.5708rad)
  Support = -> [XZ_Plane004]
  sketch-geometry (19):
    g0: LineSegment StartX=-4.7625 StartY=0 StartZ=0 EndX=4.7625 EndY=0 EndZ=0
    g1: LineSegment StartX=-4.7625 StartY=0 StartZ=0 EndX=-4.7625 EndY=-0.2921 EndZ=0
    g2: LineSegment StartX=4.7625 StartY=0 StartZ=0 EndX=4.7625 EndY=-0.2921 EndZ=0
    g3: GeomPoint X=-4.7625 Y=0.2921 Z=0
    g4: ArcOfCircle CenterX=-4.7625 CenterY=-0.8001 CenterZ=0 NormalX=0 NormalY=0 NormalZ=1 AngleXU=0 Radius=0.508 StartAngle=2e-16 EndAngle=1.5708
    g5: LineSegment StartX=-4.2545 StartY=-0.8001 StartZ=0 EndX=-4.2545 EndY=-1.0795 EndZ=0
    g6: ArcOfCircle CenterX=-3.7465 CenterY=-1.0795 CenterZ=0 NormalX=0 NormalY=0 NormalZ=1 AngleXU=0 Radius=0.508 StartAngle=3.14159 EndAngle=4.71239
    g7: LineSegment StartX=-3.7465 StartY=-1.5875 StartZ=0 EndX=-2.4765 EndY=-1.5875 EndZ=0
    g8: ArcOfCircle CenterX=-2.4765 CenterY=-1.0795 CenterZ=0 NormalX=0 NormalY=0 NormalZ=1 AngleXU=0 Radius=0.508 StartAngle=4.71239 EndAngle=5.43512
    g9: ArcOfCircle CenterX=-1.80448 CenterY=-1.8415 CenterZ=0 NormalX=0 NormalY=0 NormalZ=1 AngleXU=0 Radius=0.508 StartAngle=1.5708 EndAngle=2.29353
    g10: LineSegment StartX=-1.80448 StartY=-1.3335 StartZ=0 EndX=1.80448 EndY=-1.3335 EndZ=0
    g11: ArcOfCircle CenterX=1.80448 CenterY=-1.8415 CenterZ=0 NormalX=0 NormalY=0 NormalZ=1 AngleXU=0 Radius=0.508 StartAngle=0.848062 EndAngle=1.5708
    g12: ArcOfCircle CenterX=2.4765 CenterY=-1.0795 CenterZ=0 NormalX=0 NormalY=0 NormalZ=1 AngleXU=0 Radius=0.508 StartAngle=3.98965 EndAngle=4.71239
    g13: LineSegment StartX=2.4765 StartY=-1.5875 StartZ=0 EndX=3.7465 EndY=-1.5875 EndZ=0
    g14: ArcOfCircle CenterX=3.7465 CenterY=-1.0795 CenterZ=0 NormalX=0 NormalY=0 NormalZ=1 AngleXU=0 Radius=0.508 StartAngle=4.71239 EndAngle=6.28319
    g15: LineSegment StartX=4.2545 StartY=-1.0795 StartZ=0 EndX=4.2545 EndY=-0.8001 EndZ=0
    g16: ArcOfCircle CenterX=4.7625 CenterY=-0.8001 CenterZ=0 NormalX=0 NormalY=0 NormalZ=1 AngleXU=0 Radius=0.508 StartAngle=1.5708 EndAngle=3.14159
    g17: GeomPoint X=-3.7465 Y=1.5875 Z=0
    g18: GeomPoint X=-1.80448 Y=1.3335 Z=0
  constraints (45):
    c: Horizontal(g0)
    c: Symmetric(g0,g0,g-1)
    c: Coincident(g1,g0)
    c: Vertical(g1)
    c: Coincident(g2,g0)
    c: Vertical(g2)
    c: Symmetric(g3,g1,g-1)
    c: DistanceY(g1,g3) = 0.5842
    c: DistanceX(g3,g0) = 9.525
    c: Equal(g1,g2)
    c: Perpendicular(g1,g4) = 4.71239
    c: Tangent(g4,g5) = 1.5708
    c: Tangent(g5,g6) = -1.5708
    c: Tangent(g6,g7) = -1.5708
    c: Tangent(g7,g8) = -1.5708
    c: Tangent(g8,g9) = 1.5708
    c: Tangent(g9,g10) = 1.5708
    c: Tangent(g10,g11) = 1.5708
    c: Tangent(g11,g12) = 1.5708
    c: Tangent(g12,g13) = -1.5708
    c: Tangent(g13,g14) = -1.5708
    c: Tangent(g14,g15) = -1.5708
    c: Tangent(g15,g16) = 1.5708
    c: Vertical(g5)
    c: Horizontal(g7)
    c: Horizontal(g10)
    c: Vertical(g15)
    c: Equal(g4,g6)
    c: Equal(g8,g6)
    c: Equal(g6,g9)
    c: Equal(g6,g11)
    c: Equal(g12,g6)
    c: Equal(g6,g14)
    c: Equal(g16,g6)
    c: Radius(g6) = 0.508
    c: Symmetric(g17,g6,g-1)
    c: DistanceY(g6,g17) = 3.175
    c: Symmetric(g18,g9,g-1)
    c: DistanceY(g9,g18) = 2.667
    c: DistanceX(g7,g7) = 1.27
    c: Horizontal(g13)
    c: PointOnObject(g7,g13)
    c: Equal(g13,g7)
    c: Coincident(g16,g2)
    c: PointOnObject(g16,g2)
FEATURE [PartDesign::Revolution] Revolution002
  Angle = 360
  Axis = (1,0,0)
  Base = (0,0,0)
  Placement = pos=(0,0,0) rot=(1,0,0;1.5708rad)
  Profile = -> Sketch012
  ReferenceAxis = -> Sketch012 [H_Axis]
  Reversed = true
FEATURE [Sketcher::SketchObject] Sketch013
  FullyConstrained = true
  MapMode = 5
  Placement = pos=(0,0,0) rot=(0.57735,0.57735,0.57735;2.0944rad)
  Support = -> [YZ_Plane005]
  sketch-geometry (9):
    g0: LineSegment StartX=-3.81 StartY=0 StartZ=0 EndX=-3.81 EndY=1.5875 EndZ=0
    g1: ArcOfCircle CenterX=-2.84607 CenterY=1.5875 CenterZ=0 NormalX=0 NormalY=0 NormalZ=1 AngleXU=0 Radius=0.96393 StartAngle=1.5708 EndAngle=3.14159
    g2: LineSegment StartX=-2.84607 StartY=2.55143 StartZ=0 EndX=2.84607 EndY=2.55143 EndZ=0
    g3: ArcOfCircle CenterX=2.84607 CenterY=1.5875 CenterZ=0 NormalX=0 NormalY=0 NormalZ=1 AngleXU=0 Radius=0.96393 StartAngle=2e-16 EndAngle=1.5708
    g4: LineSegment StartX=3.81 StartY=1.5875 StartZ=0 EndX=3.81 EndY=-2e-16 EndZ=0
    g5: ArcOfCircle CenterX=2.84607 CenterY=1e-16 CenterZ=0 NormalX=0 NormalY=0 NormalZ=1 AngleXU=0 Radius=0.96393 StartAngle=4.71239 EndAngle=6.28319
    g6: LineSegment StartX=2.84607 StartY=-0.96393 StartZ=0 EndX=2.23393 EndY=-0.96393 EndZ=0
    g7: ArcOfCircle CenterX=2.23393 CenterY=1e-16 CenterZ=0 NormalX=0 NormalY=0 NormalZ=1 AngleXU=0 Radius=0.96393 StartAngle=3.14159 EndAngle=4.71239
    g8: LineSegment StartX=1.27 StartY=0 StartZ=0 EndX=1.27 EndY=1.5875 EndZ=0
  constraints (23):
    c: Tangent(g0,g1) = 1.5708
    c: Tangent(g1,g2) = 1.5708
    c: Tangent(g2,g3) = 1.5708
    c: Tangent(g3,g4) = 1.5708
    c: Vertical(g4)
    c: Horizontal(g2)
    c: Symmetric(g1,g3,g-2)
    c: Radius(g1) = 0.96393
    c: DistanceX(g0,g4) = 7.62
    c: PointOnObject(g4,g-1)
    c: Tangent(g4,g5) = 1.5708
    c: Tangent(g5,g6) = 1.5708
    c: Tangent(g6,g7) = 1.5708
    c: Tangent(g7,g8) = 1.5708
    c: Equal(g1,g5)
    c: Equal(g7,g1)
    c: Horizontal(g6)
    c: Vertical(g8)
    c: DistanceX(g7,g4) = 2.54
    c: Horizontal(g1,g8)
    c: Vertical(g0)
    c: DistanceY(g-1,g0) = 1.5875
    c: PointOnObject(g0,g-1)
FEATURE [Sketcher::SketchObject] Sketch014
  FullyConstrained = true
  MapMode = 45
  Placement = pos=(-6e-16,0,2.55143) rot=(0,0.707107,0.707107;3.14159rad)
  Support = -> [Sketch013]
  sketch-geometry (1):
    g0: Circle CenterX=0 CenterY=0 CenterZ=0 NormalX=0 NormalY=0 NormalZ=1 AngleXU=0 Radius=0.32131
  constraints (2):
    c: Coincident(g0,g-1)
    c: Diameter(g0) = 0.64262
FEATURE [PartDesign::AdditivePipe] AdditivePipe
  AuxilleryCurvelinear = true
  AuxillerySpineTangent = false
  Binormal = (0,0,0)
  Mode = 0
  Placement = pos=(0,0,0) rot=(0.57735,0.57735,0.57735;2.0944rad)
  Profile = -> Sketch014
  Spine = -> Sketch013
  SpineTangent = false
  Transformation = 0
  Transition = 0
FEATURE [PartDesign::Body] Body005  label="Body"
  Group = -> [Sketch013,Sketch014,AdditivePipe]
  Origin = -> Origin005
  Tip = -> AdditivePipe
FEATURE [Sketcher::SketchObject] Sketch015
  FullyConstrained = true
  MapMode = 5
  Placement = pos=(0,0,0) rot=(1,0,0;1.5708rad)
  Support = -> [XZ_Plane007]
  sketch-geometry (1):
    g0: Circle CenterX=0 CenterY=0 CenterZ=0 NormalX=0 NormalY=0 NormalZ=1 AngleXU=0 Radius=0.762
  constraints (2):
    c: Coincident(g0,g-1)
    c: Diameter(g0) = 1.524
FEATURE [PartDesign::Pad] Pad007
  Direction = (0,-1,-2e-16)
  Length = 5.69214
  Length2 = 10
  Midplane = true
  Placement = pos=(0,0,0) rot=(1,0,0;1.5708rad)
  Profile = -> Sketch015
  ReferenceAxis = -> Sketch015 [N_Axis]
  Type = 0
FEATURE [PartDesign::Body] Body006
  Group = -> [Sketch015,Pad007]
  Origin = -> Origin007
  Placement = pos=(0,0,2.55143) rot=(0,0,1;0rad)
  Tip = -> Pad007
FEATURE [App::Part] Part  label="Wire, Return"
  Group = -> [Body005,Body006]
  Origin = -> Origin006
  Placement = pos=(-10.16,0,0) rot=(0,0,1;0rad)
FEATURE [Sketcher::SketchObject] Sketch016
  FullyConstrained = true
  MapMode = 5
  Placement = pos=(0,0,0) rot=(0.57735,0.57735,0.57735;2.0944rad)
  Support = -> [YZ_Plane008]
  sketch-geometry (5):
    g0: LineSegment StartX=-3.81 StartY=0 StartZ=0 EndX=-3.81 EndY=1.5875 EndZ=0
    g1: ArcOfCircle CenterX=-2.84607 CenterY=1.5875 CenterZ=0 NormalX=0 NormalY=0 NormalZ=1 AngleXU=0 Radius=0.96393 StartAngle=1.5708 EndAngle=3.14159
    g2: LineSegment StartX=-2.84607 StartY=2.55143 StartZ=0 EndX=2.84607 EndY=2.55143 EndZ=0
    g3: ArcOfCircle CenterX=2.84607 CenterY=1.5875 CenterZ=0 NormalX=0 NormalY=0 NormalZ=1 AngleXU=0 Radius=0.96393 StartAngle=1e-16 EndAngle=1.5708
    g4: LineSegment StartX=3.81 StartY=1.5875 StartZ=0 EndX=3.81 EndY=0 EndZ=0
  constraints (13):
    c: Tangent(g0,g1) = 1.5708
    c: Tangent(g1,g2) = 1.5708
    c: Tangent(g2,g3) = 1.5708
    c: Tangent(g3,g4) = 1.5708
    c: Vertical(g4)
    c: Horizontal(g2)
    c: Symmetric(g1,g3,g-2)
    c: Equal(g0,g4)
    c: Radius(g1) = 0.96393
    c: DistanceX(g0,g4) = 7.62
    c: Vertical(g0)
    c: PointOnObject(g0,g-1)
    c: DistanceY(g0,g0) = 1.5875
FEATURE [Sketcher::SketchObject] Sketch017
  FullyConstrained = true
  MapMode = 45
  Placement = pos=(-6e-16,4e-16,2.55143) rot=(0,0.707107,0.707107;3.14159rad)
  Support = -> [Sketch016]
  sketch-geometry (1):
    g0: Circle CenterX=0 CenterY=0 CenterZ=0 NormalX=0 NormalY=0 NormalZ=1 AngleXU=0 Radius=0.32131
  constraints (2):
    c: Coincident(g0,g-1)
    c: Diameter(g0) = 0.64262
FEATURE [PartDesign::AdditivePipe] AdditivePipe001
  AuxilleryCurvelinear = true
  AuxillerySpineTangent = false
  Binormal = (0,0,0)
  Mode = 0
  Placement = pos=(0,0,0) rot=(0.57735,0.57735,0.57735;2.0944rad)
  Profile = -> Sketch017
  Spine = -> Sketch016
  SpineTangent = false
  Transformation = 0
  Transition = 0
FEATURE [PartDesign::Body] Body007
  Group = -> [Sketch016,Sketch017,AdditivePipe001]
  Origin = -> Origin008
  Tip = -> AdditivePipe001
FEATURE [Sketcher::SketchObject] Sketch018
  FullyConstrained = true
  MapMode = 5
  Placement = pos=(0,0,0) rot=(1,0,0;1.5708rad)
  Support = -> [XZ_Plane010]
  sketch-geometry (1):
    g0: Circle CenterX=0 CenterY=0 CenterZ=0 NormalX=0 NormalY=0 NormalZ=1 AngleXU=0 Radius=0.762
  constraints (2):
    c: Coincident(g0,g-1)
    c: Diameter(g0) = 1.524
FEATURE [PartDesign::Pad] Pad008
  Direction = (0,-1,2e-16)
  Length = 5.69214
  Length2 = 10
  Midplane = true
  Placement = pos=(0,0,0) rot=(1,0,0;1.5708rad)
  Profile = -> Sketch018
  ReferenceAxis = -> Sketch018 [N_Axis]
  Type = 0
FEATURE [PartDesign::Body] Body008
  Group = -> [Sketch018,Pad008]
  Origin = -> Origin010
  Placement = pos=(0,0,2.55143) rot=(0,0,1;0rad)
  Tip = -> Pad008
FEATURE [App::Part] Part001  label="Wire, Power"
  Group = -> [Body007,Body008]
  Origin = -> Origin009
  Placement = pos=(-12.7,0,0) rot=(0,0,1;0rad)
FEATURE [Sketcher::SketchObject] Sketch019
  FullyConstrained = true
  MapMode = 5
  Placement = pos=(0,0,0) rot=(1,0,0;1.5708rad)
  Support = -> [XZ_Plane011]
  sketch-geometry (17):
    g0: LineSegment StartX=-3.556 StartY=0 StartZ=0 EndX=3.556 EndY=0 EndZ=0
    g1: LineSegment StartX=-3.556 StartY=0 StartZ=0 EndX=-3.556 EndY=-0.2921 EndZ=0
    g2: LineSegment StartX=3.556 StartY=0 StartZ=0 EndX=3.556 EndY=-0.2921 EndZ=0
    g3: GeomPoint X=-3.556 Y=0.2921 Z=0
    g4: ArcOfCircle CenterX=-3.556 CenterY=-0.71755 CenterZ=0 NormalX=0 NormalY=0 NormalZ=1 AngleXU=0 Radius=0.42545 StartAngle=1e-16 EndAngle=1.5708
    g5: ArcOfCircle CenterX=-2.7051 CenterY=-0.71755 CenterZ=0 NormalX=0 NormalY=0 NormalZ=1 AngleXU=0 Radius=0.42545 StartAngle=3.14159 EndAngle=4.71239
    g6: LineSegment StartX=-2.7051 StartY=-1.143 StartZ=0 EndX=-1.9431 EndY=-1.143 EndZ=0
    g7: GeomPoint X=-2.7051 Y=1.143 Z=0
    g8: ArcOfCircle CenterX=3.556 CenterY=-0.71755 CenterZ=0 NormalX=0 NormalY=0 NormalZ=1 AngleXU=0 Radius=0.42545 StartAngle=1.5708 EndAngle=3.14159
    g9: ArcOfCircle CenterX=2.7051 CenterY=-0.71755 CenterZ=0 NormalX=0 NormalY=0 NormalZ=1 AngleXU=0 Radius=0.42545 StartAngle=4.71239 EndAngle=6.28319
    g10: LineSegment StartX=2.7051 StartY=-1.143 StartZ=0 EndX=1.9431 EndY=-1.143 EndZ=0
    g11: ArcOfCircle CenterX=-1.9431 CenterY=-0.71755 CenterZ=0 NormalX=0 NormalY=0 NormalZ=1 AngleXU=0 Radius=0.42545 StartAngle=4.71239 EndAngle=5.3947
    g12: ArcOfCircle CenterX=-1.40653 CenterY=-1.37795 CenterZ=0 NormalX=0 NormalY=0 NormalZ=1 AngleXU=0 Radius=0.42545 StartAngle=1.5708 EndAngle=2.2531
    g13: LineSegment StartX=-1.40653 StartY=-0.9525 StartZ=0 EndX=1.40653 EndY=-0.9525 EndZ=0
    g14: ArcOfCircle CenterX=1.40653 CenterY=-1.37795 CenterZ=0 NormalX=0 NormalY=0 NormalZ=1 AngleXU=0 Radius=0.42545 StartAngle=0.888488 EndAngle=1.5708
    g15: ArcOfCircle CenterX=1.9431 CenterY=-0.71755 CenterZ=0 NormalX=0 NormalY=0 NormalZ=1 AngleXU=0 Radius=0.42545 StartAngle=4.03008 EndAngle=4.71239
    g16: GeomPoint X=-1.40653 Y=0.9525 Z=0
  constraints (40):
    c: Horizontal(g0)
    c: Symmetric(g0,g0,g-1)
    c: Coincident(g1,g0)
    c: Vertical(g1)
    c: Coincident(g2,g0)
    c: Vertical(g2)
    c: Equal(g2,g1)
    c: Symmetric(g3,g1,g-1)
    c: DistanceY(g1,g3) = 0.5842
    c: DistanceX(g3,g0) = 7.112
    c: Perpendicular(g1,g4) = 4.71239
    c: Tangent(g5,g6) = -1.5708
    c: Horizontal(g6)
    c: Equal(g4,g5)
    c: Symmetric(g7,g5,g-1)
    c: DistanceY(g5,g7) = 2.286
    c: Tangent(g4,g5) = 1.5708
    c: Horizontal(g4,g5)
    c: Perpendicular(g2,g8) = 4.71239
    c: Tangent(g8,g9) = 1.5708
    c: Tangent(g9,g10) = 1.5708
    c: Horizontal(g9,g8)
    c: Horizontal(g10)
    c: Equal(g4,g9)
    c: Equal(g8,g4)
    c: Equal(g6,g10)
    c: Tangent(g6,g11) = -1.5708
    c: Tangent(g11,g12) = 1.5708
    c: Tangent(g12,g13) = 1.5708
    c: Tangent(g13,g14) = 1.5708
    c: Tangent(g14,g15) = 1.5708
    c: Horizontal(g13)
    c: Symmetric(g16,g12,g-1)
    c: DistanceY(g12,g16) = 1.905
    c: Equal(g11,g4)
    c: Equal(g4,g12)
    c: Equal(g14,g4)
    c: Equal(g4,g15)
    c: Tangent(g10,g15) = 1.5708
    c: DistanceX(g6,g6) = 0.762
FEATURE [PartDesign::Revolution] Revolution003
  Angle = 360
  Axis = (1,0,0)
  Base = (0,0,0)
  Placement = pos=(0,0,0) rot=(1,0,0;1.5708rad)
  Profile = -> Sketch019
  ReferenceAxis = -> Sketch019 [H_Axis]
  Reversed = true
FEATURE [Sketcher::SketchObject] Sketch020
  FullyConstrained = true
  MapMode = 5
  Placement = pos=(0,0,0) rot=(0.57735,0.57735,0.57735;2.0944rad)
  Support = -> [YZ_Plane012]
  sketch-geometry (5):
    g0: LineSegment StartX=-2.54 StartY=0 StartZ=0 EndX=-2.54 EndY=1.5875 EndZ=0
    g1: ArcOfCircle CenterX=-1.57607 CenterY=1.5875 CenterZ=0 NormalX=0 NormalY=0 NormalZ=1 AngleXU=0 Radius=0.96393 StartAngle=1.5708 EndAngle=3.14159
    g2: LineSegment StartX=-1.57607 StartY=2.55143 StartZ=0 EndX=1.57607 EndY=2.55143 EndZ=0
    g3: ArcOfCircle CenterX=1.57607 CenterY=1.5875 CenterZ=0 NormalX=0 NormalY=0 NormalZ=1 AngleXU=0 Radius=0.96393 StartAngle=0 EndAngle=1.5708
    g4: LineSegment StartX=2.54 StartY=1.5875 StartZ=0 EndX=2.54 EndY=0 EndZ=0
  constraints (13):
    c: Tangent(g0,g1) = 1.5708
    c: Tangent(g1,g2) = 1.5708
    c: Tangent(g2,g3) = 1.5708
    c: Tangent(g3,g4) = 1.5708
    c: Vertical(g4)
    c: Horizontal(g2)
    c: Symmetric(g1,g3,g-2)
    c: Equal(g0,g4)
    c: Radius(g1) = 0.96393
    c: DistanceX(g0,g4) = 5.08
    c: Vertical(g0)
    c: PointOnObject(g0,g-1)
    c: DistanceY(g0,g0) = 1.5875
FEATURE [Sketcher::SketchObject] Sketch021
  FullyConstrained = true
  MapMode = 45
  Placement = pos=(-6e-16,7e-16,2.55143) rot=(0,0.707107,0.707107;3.14159rad)
  Support = -> [Sketch020]
  sketch-geometry (1):
    g0: Circle CenterX=0 CenterY=0 CenterZ=0 NormalX=0 NormalY=0 NormalZ=1 AngleXU=0 Radius=0.32131
  constraints (2):
    c: Coincident(g0,g-1)
    c: Diameter(g0) = 0.64262
FEATURE [PartDesign::AdditivePipe] AdditivePipe002
  AuxilleryCurvelinear = true
  AuxillerySpineTangent = false
  Binormal = (0,0,0)
  Mode = 0
  Placement = pos=(0,0,0) rot=(0.57735,0.57735,0.57735;2.0944rad)
  Profile = -> Sketch021
  Spine = -> Sketch020
  SpineTangent = false
  Transformation = 0
  Transition = 0
FEATURE [PartDesign::Body] Body010
  Group = -> [Sketch020,Sketch021,AdditivePipe002]
  Origin = -> Origin012
  Tip = -> AdditivePipe002
FEATURE [Sketcher::SketchObject] Sketch022
  FullyConstrained = true
  MapMode = 5
  Placement = pos=(0,0,0) rot=(1,0,0;1.5708rad)
  Support = -> [XZ_Plane014]
  sketch-geometry (1):
    g0: Circle CenterX=0 CenterY=0 CenterZ=0 NormalX=0 NormalY=0 NormalZ=1 AngleXU=0 Radius=0.762
  constraints (2):
    c: Coincident(g0,g-1)
    c: Diameter(g0) = 1.524
FEATURE [PartDesign::Pad] Pad009
  Direction = (0,-1,-2e-16)
  Length = 3.15214
  Length2 = 10
  Midplane = true
  Placement = pos=(0,0,0) rot=(1,0,0;1.5708rad)
  Profile = -> Sketch022
  ReferenceAxis = -> Sketch022 [N_Axis]
  Type = 0
FEATURE [PartDesign::Body] Body011
  Group = -> [Sketch022,Pad009]
  Origin = -> Origin014
  Placement = pos=(0,0,2.55143) rot=(0,0,1;0rad)
  Tip = -> Pad009
FEATURE [App::Part] Part002  label="Wire, Detect"
  Group = -> [Body010,Body011]
  Origin = -> Origin013
  Placement = pos=(-15.24,1.27,0) rot=(0,0,1;0rad)
FEATURE [Sketcher::SketchObject] Sketch023
  FullyConstrained = true
  MapMode = 5
  Placement = pos=(0,0,0) rot=(0.57735,0.57735,0.57735;2.0944rad)
  Support = -> [YZ_Plane015]
  sketch-geometry (7):
    g0: LineSegment StartX=-4.01609 StartY=-1.5875 StartZ=0 EndX=-4.01609 EndY=0 EndZ=0
    g1: LineSegment StartX=4.01609 StartY=-2e-16 StartZ=0 EndX=4.01609 EndY=-1.5875 EndZ=0
    g2: ArcOfCircle CenterX=-3.05216 CenterY=-1.5875 CenterZ=0 NormalX=0 NormalY=0 NormalZ=1 AngleXU=0 Radius=0.96393 StartAngle=3.14159 EndAngle=4.71239
    g3: LineSegment StartX=-3.05216 StartY=-2.55143 StartZ=0 EndX=3.05216 EndY=-2.55143 EndZ=0
    g4: ArcOfCircle CenterX=3.05216 CenterY=-1.5875 CenterZ=0 NormalX=0 NormalY=0 NormalZ=1 AngleXU=0 Radius=0.96393 StartAngle=4.71239 EndAngle=6.28319
    g5: LineSegment StartX=-4.01609 StartY=0 StartZ=0 EndX=3.21287 EndY=2.40966 EndZ=0
    g6: LineSegment StartX=3.21287 StartY=2.40966 StartZ=0 EndX=4.01609 EndY=0 EndZ=0
  constraints (18):
    c: Vertical(g1)
    c: DistanceY(g0,g-1) = 1.5875
    c: Equal(g0,g1)
    c: Tangent(g0,g2) = 1.5708
    c: Tangent(g2,g3) = -1.5708
    c: Tangent(g3,g4) = -1.5708
    c: Radius(g2) = 0.96393
    c: Horizontal(g3)
    c: Tangent(g4,g1) = 1.5708
    c: Symmetric(g2,g4,g-2)
    c: Coincident(g0,g5)
    c: Coincident(g5,g6)
    c: Coincident(g6,g1)
    c: Perpendicular(g5,g6)
    c: Distance(g6) = 2.54
    c: Distance(g5) = 7.62
    c: PointOnObject(g0,g-1)
    c: Vertical(g0)
FEATURE [Sketcher::SketchObject] Sketch024
  FullyConstrained = true
  MapMode = 45
  Placement = pos=(6e-16,-4e-16,-2.55143) rot=(0,0.707107,0.707107;3.14159rad)
  Support = -> [Sketch023]
  sketch-geometry (1):
    g0: Circle CenterX=0 CenterY=0 CenterZ=0 NormalX=0 NormalY=0 NormalZ=1 AngleXU=0 Radius=0.32131
  constraints (2):
    c: Coincident(g0,g-1)
    c: Diameter(g0) = 0.64262
FEATURE [PartDesign::AdditivePipe] AdditivePipe003
  AuxilleryCurvelinear = true
  AuxillerySpineTangent = false
  Binormal = (0,0,0)
  Mode = 0
  Placement = pos=(0,0,0) rot=(0.57735,0.57735,0.57735;2.0944rad)
  Profile = -> Sketch024
  Spine = -> Sketch023
  SpineTangent = false
  Transformation = 0
  Transition = 0
FEATURE [PartDesign::Body] Body012
  Group = -> [Sketch023,Sketch024,AdditivePipe003]
  Origin = -> Origin015
  Tip = -> AdditivePipe003
FEATURE [Sketcher::SketchObject] Sketch025
  FullyConstrained = true
  MapMode = 5
  Placement = pos=(0,0,0) rot=(1,0,0;1.5708rad)
  Support = -> [XZ_Plane017]
  sketch-geometry (1):
    g0: Circle CenterX=0 CenterY=0 CenterZ=0 NormalX=0 NormalY=0 NormalZ=1 AngleXU=0 Radius=0.762
  constraints (2):
    c: Coincident(g0,g-1)
    c: Diameter(g0) = 1.524
FEATURE [PartDesign::Pad] Pad010
  Direction = (0,-1,-2e-16)
  Length = 6.10433
  Length2 = 10
  Midplane = true
  Placement = pos=(0,0,0) rot=(1,0,0;1.5708rad)
  Profile = -> Sketch025
  ReferenceAxis = -> Sketch025 [N_Axis]
  Type = 0
FEATURE [PartDesign::Body] Body013
  Group = -> [Sketch025,Pad010]
  Origin = -> Origin017
  Placement = pos=(0,0,-2.55143) rot=(0,0,1;0rad)
  Tip = -> Pad010
FEATURE [App::Part] Part003  label="Wire, LED jumper"
  Group = -> [Body012,Body013]
  Origin = -> Origin016
  Placement = pos=(-3.81,0,1.5875) rot=(0,0,1;-0.321751rad)
FEATURE [Sketcher::SketchObject] Sketch026
  FullyConstrained = true
  MapMode = 5
  Placement = pos=(0,0,0) rot=(0.57735,0.57735,0.57735;2.0944rad)
  Support = -> [YZ_Plane018]
  sketch-geometry (5):
    g0: LineSegment StartX=-5.08 StartY=0 StartZ=0 EndX=-5.08 EndY=1.5875 EndZ=0
    g1: ArcOfCircle CenterX=-4.11607 CenterY=1.5875 CenterZ=0 NormalX=0 NormalY=0 NormalZ=1 AngleXU=0 Radius=0.96393 StartAngle=1.5708 EndAngle=3.14159
    g2: LineSegment StartX=-4.11607 StartY=2.55143 StartZ=0 EndX=4.11607 EndY=2.55143 EndZ=0
    g3: ArcOfCircle CenterX=4.11607 CenterY=1.5875 CenterZ=0 NormalX=0 NormalY=0 NormalZ=1 AngleXU=0 Radius=0.96393 StartAngle=1e-16 EndAngle=1.5708
    g4: LineSegment StartX=5.08 StartY=1.5875 StartZ=0 EndX=5.08 EndY=0 EndZ=0
  constraints (13):
    c: Tangent(g0,g1) = 1.5708
    c: Tangent(g1,g2) = 1.5708
    c: Tangent(g2,g3) = 1.5708
    c: Tangent(g3,g4) = 1.5708
    c: Vertical(g4)
    c: Horizontal(g2)
    c: Symmetric(g1,g3,g-2)
    c: Equal(g0,g4)
    c: Radius(g1) = 0.96393
    c: DistanceX(g0,g4) = 10.16
    c: PointOnObject(g0,g-1)
    c: Vertical(g0)
    c: DistanceY(g0,g0) = 1.5875
FEATURE [Sketcher::SketchObject] Sketch027
  FullyConstrained = true
  MapMode = 45
  Placement = pos=(-6e-16,9e-16,2.55143) rot=(0,0.707107,0.707107;3.14159rad)
  Support = -> [Sketch026]
  sketch-geometry (1):
    g0: Circle CenterX=0 CenterY=0 CenterZ=0 NormalX=0 NormalY=0 NormalZ=1 AngleXU=0 Radius=0.32131
  constraints (2):
    c: Coincident(g0,g-1)
    c: Diameter(g0) = 0.64262
FEATURE [PartDesign::AdditivePipe] AdditivePipe004
  AuxilleryCurvelinear = true
  AuxillerySpineTangent = false
  Binormal = (0,0,0)
  Mode = 0
  Placement = pos=(0,0,0) rot=(0.57735,0.57735,0.57735;2.0944rad)
  Profile = -> Sketch027
  Spine = -> Sketch026
  SpineTangent = false
  Transformation = 0
  Transition = 0
FEATURE [PartDesign::Body] Body014
  Group = -> [Sketch026,Sketch027,AdditivePipe004]
  Origin = -> Origin018
  Tip = -> AdditivePipe004
FEATURE [Sketcher::SketchObject] Sketch028
  FullyConstrained = true
  MapMode = 5
  Placement = pos=(0,0,0) rot=(1,0,0;1.5708rad)
  Support = -> [XZ_Plane020]
  sketch-geometry (1):
    g0: Circle CenterX=0 CenterY=0 CenterZ=0 NormalX=0 NormalY=0 NormalZ=1 AngleXU=0 Radius=0.762
  constraints (2):
    c: Coincident(g0,g-1)
    c: Diameter(g0) = 1.524
FEATURE [PartDesign::Pad] Pad011
  Direction = (0,-1,-2e-16)
  Length = 8.23214
  Length2 = 10
  Midplane = true
  Placement = pos=(0,0,0) rot=(1,0,0;1.5708rad)
  Profile = -> Sketch028
  ReferenceAxis = -> Sketch028 [N_Axis]
  Type = 0
FEATURE [PartDesign::Body] Body015
  Group = -> [Sketch028,Pad011]
  Origin = -> Origin020
  Placement = pos=(0,0,2.55143) rot=(0,0,1;0rad)
  Tip = -> Pad011
FEATURE [App::Part] Part004  label="Wire, Switch"
  Group = -> [Body014,Body015]
  Origin = -> Origin019
  Placement = pos=(-12.7,8.89,0) rot=(0,0,1;1.5708rad)
FEATURE [Sketcher::SketchObject] Sketch029
  ExternalGeometry = -> [Sketch012]
  FullyConstrained = true
  MapMode = 5
  Placement = pos=(0,0,0) rot=(0.57735,0.57735,0.57735;2.0944rad)
  Support = -> [YZ_Plane004]
  sketch-geometry (1):
    g0: Circle CenterX=0 CenterY=0 CenterZ=0 NormalX=0 NormalY=0 NormalZ=1 AngleXU=0 Radius=0.2921
  constraints (2):
    c: Coincident(g0,g-3)
    c: PointOnObject(g-3,g0)
FEATURE [Sketcher::SketchObject] Sketch030
  ExternalGeometry = -> [Sketch012]
  FullyConstrained = true
  MapMode = 5
  Placement = pos=(0,0,0) rot=(1,0,0;1.5708rad)
  Support = -> [XZ_Plane004]
  sketch-geometry (9):
    g0: ArcOfCircle CenterX=-4.7625 CenterY=-0.8763 CenterZ=0 NormalX=0 NormalY=0 NormalZ=1 AngleXU=0 Radius=0.8763 StartAngle=1.5708 EndAngle=3.96304
    g1: LineSegment StartX=-4.7625 StartY=0 StartZ=0 EndX=4.7625 EndY=-1.2e-15 EndZ=0
    g2: ArcOfCircle CenterX=4.7625 CenterY=-0.8763 CenterZ=0 NormalX=0 NormalY=0 NormalZ=1 AngleXU=0 Radius=0.8763 StartAngle=5.46173 EndAngle=7.85398
    g3: ArcOfCircle CenterX=-5.9563 CenterY=-2.15944 CenterZ=0 NormalX=0 NormalY=0 NormalZ=1 AngleXU=0 Radius=0.8763 StartAngle=0 EndAngle=0.821451
    g4: LineSegment StartX=-5.08 StartY=-2.15944 StartZ=0 EndX=-5.08 EndY=-5.33444 EndZ=0
    g5: ArcOfCircle CenterX=5.9563 CenterY=-2.15944 CenterZ=0 NormalX=0 NormalY=0 NormalZ=1 AngleXU=0 Radius=0.8763 StartAngle=2.32014 EndAngle=3.14159
    g6: LineSegment StartX=5.08 StartY=-2.15944 StartZ=0 EndX=5.08 EndY=-5.33444 EndZ=0
    g7: LineSegment StartX=-4.7625 StartY=-0.2921 StartZ=0 EndX=-4.7625 EndY=-0.5842 EndZ=0
    g8: LineSegment StartX=-4.7625 StartY=-0.5842 StartZ=0 EndX=-4.7625 EndY=-0.8763 EndZ=0
  constraints (24):
    c: Tangent(g0,g1) = 1.5708
    c: Tangent(g1,g2) = 1.5708
    c: Coincident(g0,g-3)
    c: Equal(g2,g0)
    c: Tangent(g0,g3) = 1.5708
    c: Tangent(g3,g4) = 1.5708
    c: Tangent(g2,g5) = 1.5708
    c: Tangent(g5,g6) = -1.5708
    c: Vertical(g6)
    c: Vertical(g4)
    c: Equal(g0,g3)
    c: Equal(g0,g5)
    c: DistanceX(g4,g6) = 10.16
    c: Equal(g4,g6)
    c: DistanceY(g4,g4) = 3.175
    c: Coincident(g-4,g7)
    c: Vertical(g7)
    c: Coincident(g7,g8)
    c: Vertical(g8)
    c: Equal(g-4,g7)
    c: Equal(g-4,g8)
    c: Coincident(g0,g8)
    c: PointOnObject(g1,g-5)
    c: Horizontal(g5,g3)
FEATURE [PartDesign::AdditivePipe] AdditivePipe005
  AuxilleryCurvelinear = true
  AuxillerySpineTangent = false
  BaseFeature = -> Revolution002
  Binormal = (0,0,0)
  Mode = 0
  Placement = pos=(0,0,0) rot=(1,0,0;1.5708rad)
  Profile = -> Sketch029
  Spine = -> Sketch030
  SpineTangent = false
  Transformation = 0
  Transition = 0
FEATURE [PartDesign::Body] Body004  label="Resistor, 15Ω"
  Group = -> [Sketch012,Revolution002,Sketch029,Sketch030,AdditivePipe005]
  Origin = -> Origin004
  Placement = pos=(-7.62,-11.43,3.74693) rot=(0,0,1;0rad)
  Tip = -> AdditivePipe005
FEATURE [Sketcher::SketchObject] Sketch031
  ExternalGeometry = -> [Sketch019]
  FullyConstrained = true
  MapMode = 5
  Placement = pos=(0,0,0) rot=(0.57735,0.57735,0.57735;2.0944rad)
  Support = -> [YZ_Plane011]
  sketch-geometry (1):
    g0: Circle CenterX=0 CenterY=0 CenterZ=0 NormalX=0 NormalY=0 NormalZ=1 AngleXU=0 Radius=0.2921
  constraints (2):
    c: Coincident(g0,g-3)
    c: PointOnObject(g-3,g0)
FEATURE [Sketcher::SketchObject] Sketch032
  ExternalGeometry = -> [Sketch019]
  FullyConstrained = true
  MapMode = 5
  Placement = pos=(0,0,0) rot=(1,0,0;1.5708rad)
  Support = -> [XZ_Plane011]
  sketch-geometry (10):
    g0: LineSegment StartX=-3.556 StartY=-0.2921 StartZ=0 EndX=-3.556 EndY=-0.5842 EndZ=0
    g1: LineSegment StartX=-3.5921 StartY=-4.74934 StartZ=0 EndX=-3.5921 EndY=-1.57434 EndZ=0
    g2: ArcOfCircle CenterX=-4.1763 CenterY=-1.57434 CenterZ=0 NormalX=0 NormalY=0 NormalZ=1 AngleXU=0 Radius=0.5842 StartAngle=-9e-16 EndAngle=1.01114
    g3: ArcOfCircle CenterX=-3.556 CenterY=-0.5842 CenterZ=0 NormalX=0 NormalY=0 NormalZ=1 AngleXU=0 Radius=0.5842 StartAngle=1.5708 EndAngle=4.15273
    g4: LineSegment StartX=-3.556 StartY=0 StartZ=0 EndX=3.556 EndY=-9e-16 EndZ=0
    g5: ArcOfCircle CenterX=3.556 CenterY=-0.5842 CenterZ=0 NormalX=0 NormalY=0 NormalZ=1 AngleXU=0 Radius=0.5842 StartAngle=5.27205 EndAngle=7.85398
    g6: ArcOfCircle CenterX=4.1763 CenterY=-1.57434 CenterZ=0 NormalX=0 NormalY=0 NormalZ=1 AngleXU=0 Radius=0.5842 StartAngle=2.13046 EndAngle=3.14159
    g7: LineSegment StartX=3.5921 StartY=-1.57434 StartZ=0 EndX=3.5921 EndY=-4.74934 EndZ=0
    g8: LineSegment StartX=-3.5921 StartY=-4.74934 StartZ=0 EndX=-1.71e-13 EndY=-1.15724 EndZ=0
    g9: LineSegment StartX=-1.71e-13 StartY=-1.15724 StartZ=0 EndX=3.5921 EndY=-4.74934 EndZ=0
  constraints (26):
    c: Coincident(g0,g-3)
    c: Vertical(g0)
    c: Equal(g-3,g0)
    c: Vertical(g1)
    c: Tangent(g1,g2) = -1.5708
    c: Tangent(g2,g3) = 1.5708
    c: Tangent(g3,g4) = 1.5708
    c: Tangent(g4,g5) = 1.5708
    c: Tangent(g5,g6) = 1.5708
    c: Tangent(g6,g7) = -1.5708
    c: Coincident(g3,g-3)
    c: Coincident(g3,g0)
    c: Vertical(g7)
    c: Equal(g3,g2)
    c: DistanceY(g1,g1) = 3.175
    c: PointOnObject(g4,g-4)
    c: Equal(g5,g3)
    c: Equal(g3,g6)
    c: Equal(g7,g1)
    c: Horizontal(g2,g6)
    c: Coincident(g1,g8)
    c: Coincident(g8,g9)
    c: Coincident(g9,g7)
    c: Equal(g9,g8)
    c: Perpendicular(g9,g8)
    c: Distance(g8) = 5.08
FEATURE [PartDesign::AdditivePipe] AdditivePipe006
  AuxilleryCurvelinear = true
  AuxillerySpineTangent = false
  BaseFeature = -> Revolution003
  Binormal = (0,0,0)
  Mode = 0
  Placement = pos=(0,0,0) rot=(1,0,0;1.5708rad)
  Profile = -> Sketch031
  Spine = -> Sketch032
  SpineTangent = false
  Transformation = 0
  Transition = 0
FEATURE [PartDesign::Body] Body009  label="Resistor, 10KΩ"
  Group = -> [Sketch019,Revolution003,Sketch031,Sketch032,AdditivePipe006]
  Origin = -> Origin011
  Placement = pos=(-15.24,-3.81,3.16184) rot=(0,0,-1;0.785398rad)
  Tip = -> AdditivePipe006
FEATURE [Sketcher::SketchObject] Sketch033
  FullyConstrained = true
  MapMode = 5
  Placement = pos=(0,0,0) rot=(1,0,0;1.5708rad)
  Support = -> [XZ_Plane022]
  sketch-geometry (1):
    g0: Circle CenterX=0 CenterY=0 CenterZ=0 NormalX=0 NormalY=0 NormalZ=1 AngleXU=0 Radius=0.32131
  constraints (2):
    c: Coincident(g0,g-1)
    c: Diameter(g0) = 0.64262
FEATURE [Sketcher::SketchObject] Sketch038
  FullyConstrained = true
  MapMode = 5
  Placement = pos=(0,0,0) rot=(1,0,0;1.5708rad)
  Support = -> [XZ_Plane023]
  sketch-geometry (1):
    g0: Circle CenterX=0 CenterY=0 CenterZ=0 NormalX=0 NormalY=0 NormalZ=1 AngleXU=0 Radius=0.762
  constraints (2):
    c: Coincident(g0,g-1)
    c: Diameter(g0) = 1.524
FEATURE [Sketcher::SketchObject] Sketch042
  FullyConstrained = true
  MapMode = 5
  Support = -> [XY_Plane024]
  sketch-geometry (4):
    g0: LineSegment StartX=-3.175 StartY=9.525 StartZ=0 EndX=3.175 EndY=9.525 EndZ=0
    g1: LineSegment StartX=3.175 StartY=9.525 StartZ=0 EndX=3.175 EndY=-9.525 EndZ=0
    g2: LineSegment StartX=3.175 StartY=-9.525 StartZ=0 EndX=-3.175 EndY=-9.525 EndZ=0
    g3: LineSegment StartX=-3.175 StartY=-9.525 StartZ=0 EndX=-3.175 EndY=9.525 EndZ=0
  constraints (11):
    c: Coincident(g0,g1)
    c: Coincident(g1,g2)
    c: Coincident(g2,g3)
    c: Coincident(g3,g0)
    c: Horizontal(g0)
    c: Horizontal(g2)
    c: Vertical(g1)
    c: Vertical(g3)
    c: Symmetric(g1,g0,g-1)
    c: DistanceX(g0,g0) = 6.35
    c: DistanceY(g3,g3) = 19.05
FEATURE [PartDesign::Pad] Pad012
  Direction = (0,0,1)
  Length = 1.5875
  Length2 = 10
  Profile = -> Sketch042
  ReferenceAxis = -> Sketch042 [N_Axis]
  Type = 0
FEATURE [Sketcher::SketchObject] Sketch044
  FullyConstrained = true
  MapMode = 5
  Support = -> [XY_Plane024]
  sketch-geometry (16):
    g0: Circle CenterX=-1.27 CenterY=6.35 CenterZ=0 NormalX=0 NormalY=0 NormalZ=1 AngleXU=0 Radius=0.79375
    g1: Circle CenterX=1.27 CenterY=6.35 CenterZ=0 NormalX=0 NormalY=0 NormalZ=1 AngleXU=0 Radius=0.79375
    g2: LineSegment StartX=-1.27 StartY=6.35 StartZ=0 EndX=1.27 EndY=6.35 EndZ=0
    g3: LineSegment StartX=1.27 StartY=-6.35 StartZ=0 EndX=-1.27 EndY=-6.35 EndZ=0
    g4: LineSegment StartX=-1.27 StartY=-6.35 StartZ=0 EndX=-1.27 EndY=6.35 EndZ=0
    g5: Circle CenterX=-1.27 CenterY=-6.35 CenterZ=0 NormalX=0 NormalY=0 NormalZ=1 AngleXU=0 Radius=0.79375
    g6: Circle CenterX=1.27 CenterY=-6.35 CenterZ=0 NormalX=0 NormalY=0 NormalZ=1 AngleXU=0 Radius=0.79375
    g7: LineSegment StartX=-1.69426 StartY=1.27 StartZ=0 EndX=-1.27 EndY=0.845736 EndZ=0
    g8: LineSegment StartX=-1.27 StartY=0.845736 StartZ=0 EndX=-0.845736 EndY=1.27 EndZ=0
    g9: LineSegment StartX=-0.845736 StartY=1.27 StartZ=0 EndX=-1.27 EndY=1.69426 EndZ=0
    g10: LineSegment StartX=-1.27 StartY=1.69426 StartZ=0 EndX=-1.69426 EndY=1.27 EndZ=0
    g11: GeomPoint X=-1.27 Y=1.27 Z=0
    g12: LineSegment StartX=-1.27 StartY=1.27 StartZ=0 EndX=0 EndY=1.27 EndZ=0
    g13: LineSegment StartX=0 StartY=1.27 StartZ=0 EndX=0 EndY=0 EndZ=0
    g14: Circle CenterX=-0.962498 CenterY=0.962498 CenterZ=0 NormalX=0 NormalY=0 NormalZ=1 AngleXU=0 Radius=0.79375
    g15: Circle CenterX=0.962498 CenterY=-0.962498 CenterZ=0 NormalX=0 NormalY=0 NormalZ=1 AngleXU=0 Radius=0.79375
  constraints (40):
    c: Equal(g0,g1)
    c: DistanceX(g0,g1) = 2.54
    c: Diameter(g0) = 1.5875
    c: Coincident(g3,g4)
    c: Coincident(g4,g2)
    c: Horizontal(g2)
    c: Horizontal(g3)
    c: Vertical(g4)
    c: Coincident(g2,g0)
    c: Symmetric(g0,g3,g-1)
    c: Coincident(g2,g1)
    c: Coincident(g5,g3)
    c: Equal(g6,g0)
    c: Equal(g0,g5)
    c: DistanceY(g4,g4) = 12.7
    c: Coincident(g3,g6)
    c: Vertical(g1,g6)
    c: Coincident(g7,g8)
    c: Coincident(g8,g9)
    c: Coincident(g9,g10)
    c: Coincident(g10,g7)
    c: Symmetric(g8,g7,g11)
    c: Perpendicular(g8,g7)
    c: Perpendicular(g8,g9)
    c: Parallel(g8,g10)
    c: Equal(g7,g10)
    c: Distance(g9) = 0.6
    c: PointOnObject(g11,g4)
    c: PointOnObject(g9,g4)
    c: Coincident(g12,g11)
    c: Horizontal(g12)
    c: Coincident(g12,g13)
    c: Coincident(g13,g-1)
    c: Vertical(g13)
    c: Equal(g13,g12)
    c: Equal(g14,g0)
    c: PointOnObject(g9,g14)
    c: PointOnObject(g7,g14)
    c: Equal(g15,g0)
    c: Symmetric(g14,g15,g13)
FEATURE [PartDesign::Pocket] Pocket003
  BaseFeature = -> Pad012
  Direction = (0,0,-1)
  Length = 5
  Length2 = 5
  Profile = -> Sketch044
  ReferenceAxis = -> Sketch044 [N_Axis]
  Reversed = true
  Type = 1
FEATURE [PartDesign::Body] Body018  label="Spacer"
  Group = -> [Sketch042,Pad012,Sketch044,Pocket003]
  Origin = -> Origin024
  Placement = pos=(-3.81,0,1.5875) rot=(0,0,1;0rad)
  Tip = -> Pocket003
FEATURE [Sketcher::SketchObject] Sketch049
  FullyConstrained = true
  MapMode = 5
  Support = -> [XY_Plane026]
  sketch-geometry (7):
    g0: LineSegment StartX=-3.175 StartY=9.525 StartZ=0 EndX=3.175 EndY=9.525 EndZ=0
    g1: LineSegment StartX=3.175 StartY=9.525 StartZ=0 EndX=3.175 EndY=-9.525 EndZ=0
    g2: LineSegment StartX=3.175 StartY=-9.525 StartZ=0 EndX=-3.175 EndY=-9.525 EndZ=0
    g3: LineSegment StartX=-3.175 StartY=-9.525 StartZ=0 EndX=-3.175 EndY=9.525 EndZ=0
    g4: Circle CenterX=0 CenterY=0 CenterZ=0 NormalX=0 NormalY=0 NormalZ=1 AngleXU=0 Radius=2.1082
    g5: Circle CenterX=0 CenterY=6.35 CenterZ=0 NormalX=0 NormalY=0 NormalZ=1 AngleXU=0 Radius=2.1082
    g6: Circle CenterX=0 CenterY=-6.35 CenterZ=0 NormalX=0 NormalY=0 NormalZ=1 AngleXU=0 Radius=2.1082
  constraints (18):
    c: Coincident(g0,g1)
    c: Coincident(g1,g2)
    c: Coincident(g2,g3)
    c: Coincident(g3,g0)
    c: Horizontal(g0)
    c: Horizontal(g2)
    c: Vertical(g1)
    c: Vertical(g3)
    c: Symmetric(g0,g1,g-1)
    c: DistanceX(g0,g0) = 6.35
    c: DistanceY(g3,g3) = 19.05
    c: Coincident(g4,g-1)
    c: PointOnObject(g5,g-2)
    c: Symmetric(g6,g5,g-1)
    c: Equal(g4,g6)
    c: Equal(g4,g5)
    c: Diameter(g4) = 4.2164
    c: DistanceY(g6,g5) = 12.7
FEATURE [PartDesign::Pad] Pad016
  Direction = (0,0,1)
  Length = 10.16
  Length2 = 10
  Profile = -> Sketch049
  ReferenceAxis = -> Sketch049 [N_Axis]
  Type = 0
FEATURE [TechDraw::DrawSVGTemplate] Template
  EditableTexts = DrawingTitle=Spacer
  Height = 200
  Orientation = 0
  Template = <userpath>/Documents/Software/FreeCAD/Templates/Nook_portrait.svg
  Width = 150
FEATURE [TechDraw::DrawSVGTemplate] Template002
  EditableTexts = DrawingTitle=Shroud
  Height = 200
  Orientation = 0
  Template = <userpath>/Documents/Software/FreeCAD/Templates/Nook_portrait.svg
  Width = 150
FEATURE [Sketcher::SketchObject] Sketch053
  FullyConstrained = true
  MapMode = 5
  Support = -> [XY_Plane030]
  sketch-geometry (12):
    g0: LineSegment StartX=-20.32 StartY=16.51 StartZ=0 EndX=20.32 EndY=16.51 EndZ=0
    g1: LineSegment StartX=26.67 StartY=10.16 StartZ=0 EndX=26.67 EndY=-10.16 EndZ=0
    g2: LineSegment StartX=20.32 StartY=-16.51 StartZ=0 EndX=-20.32 EndY=-16.51 EndZ=0
    g3: LineSegment StartX=-26.67 StartY=-10.16 StartZ=0 EndX=-26.67 EndY=10.16 EndZ=0
    g4: ArcOfCircle CenterX=-20.32 CenterY=10.16 CenterZ=0 NormalX=0 NormalY=0 NormalZ=1 AngleXU=0 Radius=6.35 StartAngle=1.5708 EndAngle=3.14159
    g5: ArcOfCircle CenterX=-20.32 CenterY=-10.16 CenterZ=0 NormalX=0 NormalY=0 NormalZ=1 AngleXU=0 Radius=6.35 StartAngle=3.14159 EndAngle=4.71239
    g6: ArcOfCircle CenterX=20.32 CenterY=-10.16 CenterZ=0 NormalX=0 NormalY=0 NormalZ=1 AngleXU=0 Radius=6.35 StartAngle=4.71239 EndAngle=6.28319
    g7: ArcOfCircle CenterX=20.32 CenterY=10.16 CenterZ=0 NormalX=0 NormalY=0 NormalZ=1 AngleXU=0 Radius=6.35 StartAngle=0 EndAngle=1.5708
    g8: Circle CenterX=-22.86 CenterY=-12.7 CenterZ=0 NormalX=0 NormalY=0 NormalZ=1 AngleXU=0 Radius=1.5875
    g9: Circle CenterX=-22.86 CenterY=12.7 CenterZ=0 NormalX=0 NormalY=0 NormalZ=1 AngleXU=0 Radius=1.5875
    g10: Circle CenterX=22.86 CenterY=12.7 CenterZ=0 NormalX=0 NormalY=0 NormalZ=1 AngleXU=0 Radius=1.5875
    g11: Circle CenterX=22.86 CenterY=-12.7 CenterZ=0 NormalX=0 NormalY=0 NormalZ=1 AngleXU=0 Radius=1.5875
  constraints (30):
    c: Horizontal(g0)
    c: Horizontal(g2)
    c: Vertical(g1)
    c: Vertical(g3)
    c: Tangent(g0,g4) = 1.5708
    c: Tangent(g3,g4) = 1.5708
    c: Tangent(g3,g5) = 1.5708
    c: Tangent(g2,g5) = 1.5708
    c: Tangent(g2,g6) = 1.5708
    c: Tangent(g1,g6) = 1.5708
    c: Tangent(g1,g7) = 1.5708
    c: Tangent(g0,g7) = 1.5708
    c: Equal(g4,g5)
    c: Equal(g4,g7)
    c: Equal(g6,g4)
    c: Symmetric(g5,g7,g-1)
    c: DistanceX(g3,g1) = 53.34
    c: DistanceY(g2,g0) = 33.02
    c: Radius(g4) = 6.35
    c: Equal(g8,g9)
    c: Equal(g8,g10)
    c: Equal(g11,g8)
    c: Symmetric(g8,g10,g-1)
    c: Vertical(g9,g8)
    c: Horizontal(g9,g10)
    c: Vertical(g10,g11)
    c: Horizontal(g11,g8)
    c: Diameter(g8) = 3.175
    c: DistanceX(g8,g11) = 45.72
    c: DistanceY(g8,g9) = 25.4
FEATURE [PartDesign::Pad] Pad017
  Direction = (0,0,1)
  Length = 1.5875
  Length2 = 10
  Profile = -> Sketch053
  ReferenceAxis = -> Sketch053 [N_Axis]
  Type = 0
FEATURE [Sketcher::SketchObject] Sketch054
  FullyConstrained = true
  MapMode = 5
  Support = -> [XY_Plane030]
  sketch-geometry (1):
    g0: Circle CenterX=-17.78 CenterY=13.97 CenterZ=0 NormalX=0 NormalY=0 NormalZ=1 AngleXU=0 Radius=0.6
  constraints (3):
    c: Diameter(g0) = 1.2
    c: DistanceX(g0,g-1) = 17.78
    c: DistanceY(g-1,g0) = 13.97
FEATURE [PartDesign::LinearPattern] LinearPattern004
  Direction = -> Sketch054 [H_Axis]
  Length = 35.56
  Occurrences = 15
FEATURE [PartDesign::LinearPattern] LinearPattern005
  Direction = -> Sketch054 [V_Axis]
  Length = 27.94
  Occurrences = 12
  Reversed = true
FEATURE [PartDesign::Pocket] Pocket006
  BaseFeature = -> Pad017
  Direction = (0,0,-1)
  Length = 5
  Length2 = 5
  Profile = -> Sketch054
  ReferenceAxis = -> Sketch054 [N_Axis]
  Reversed = true
  Type = 1
FEATURE [PartDesign::MultiTransform] MultiTransform002
  BaseFeature = -> Pocket006
  Originals = -> [Pocket006]
  Transformations = -> [LinearPattern004,LinearPattern005]
FEATURE [Sketcher::SketchObject] Sketch055
  ExternalGeometry = -> [Sketch054]
  FullyConstrained = true
  MapMode = 5
  Support = -> [XY_Plane030]
  sketch-geometry (1):
    g0: Circle CenterX=-25.4 CenterY=8.89 CenterZ=0 NormalX=0 NormalY=0 NormalZ=1 AngleXU=0 Radius=0.6
  constraints (3):
    c: Equal(g0,g-3)
    c: DistanceX(g0,g-1) = 25.4
    c: DistanceY(g-1,g0) = 8.89
FEATURE [PartDesign::LinearPattern] LinearPattern006
  Direction = -> Sketch055 [H_Axis]
  Length = 5.08
  Occurrences = 3
FEATURE [PartDesign::LinearPattern] LinearPattern007
  Direction = -> Sketch055 [V_Axis]
  Length = 17.78
  Occurrences = 8
  Reversed = true
FEATURE [PartDesign::Mirrored] Mirrored001
  MirrorPlane = -> Sketch055 [V_Axis]
FEATURE [PartDesign::Pocket] Pocket007
  BaseFeature = -> MultiTransform002
  Direction = (0,0,-1)
  Length = 5
  Length2 = 5
  Profile = -> Sketch055
  ReferenceAxis = -> Sketch055 [N_Axis]
  Reversed = true
  Type = 1
FEATURE [PartDesign::MultiTransform] MultiTransform003
  BaseFeature = -> Pocket007
  Originals = -> [Pocket007]
  Transformations = -> [LinearPattern006,LinearPattern007,Mirrored001]
FEATURE [Sketcher::SketchObject] Sketch056
  ExternalGeometry = -> [Sketch053]
  FullyConstrained = true
  MapMode = 5
  Support = -> [XY_Plane030]
  sketch-geometry (5):
    g0: LineSegment StartX=-26.67 StartY=16.51 StartZ=0 EndX=0.599999 EndY=16.51 EndZ=0
    g1: LineSegment StartX=0.599999 StartY=16.51 StartZ=0 EndX=0.599999 EndY=-16.51 EndZ=0
    g2: LineSegment StartX=0.599999 StartY=-16.51 StartZ=0 EndX=-26.67 EndY=-16.51 EndZ=0
    g3: LineSegment StartX=-26.67 StartY=-16.51 StartZ=0 EndX=-26.67 EndY=16.51 EndZ=0
    g4: Circle CenterX=22.86 CenterY=0 CenterZ=0 NormalX=0 NormalY=0 NormalZ=1 AngleXU=0 Radius=1.78435
  constraints (15):
    c: Coincident(g0,g1)
    c: Coincident(g1,g2)
    c: Coincident(g2,g3)
    c: Coincident(g3,g0)
    c: Horizontal(g0)
    c: Horizontal(g2)
    c: Vertical(g1)
    c: Vertical(g3)
    c: DistanceX(g-1,g0) = 0.599999
    c: Tangent(g-3,g0)
    c: Tangent(g-3,g3)
    c: Tangent(g-4,g2)
    c: PointOnObject(g4,g-1)
    c: Diameter(g4) = 3.5687
    c: Vertical(g-5,g4)
FEATURE [PartDesign::Pocket] Pocket008
  BaseFeature = -> MultiTransform003
  Direction = (0,0,-1)
  Length = 5
  Length2 = 5
  Profile = -> Sketch056
  ReferenceAxis = -> Sketch056 [N_Axis]
  Reversed = true
  Type = 1
FEATURE [PartDesign::Body] Body024  label="Perma-Proto, Small Mint Tin001"
  Group = -> [Sketch053,Pad017,Sketch054,Sketch055,Pocket006,MultiTransform002,LinearPattern004,LinearPattern005,Pocket007,MultiTransform003,LinearPattern006,LinearPattern007,Mirrored001,Sketch056,Pocket008]
  Origin = -> Origin030
  Tip = -> Pocket008
FEATURE [Part::FeaturePython] Clone004  label="705530003-002"  # Draft clone (typed FeaturePython)
  AttacherType = Attacher::AttachEngine3D
  Fuse = false
  Objects = -> [Part__Feature]
  Placement = pos=(13.97,21.1455,4.5085) rot=(0,0.707107,0.707107;3.14159rad)
  Scale = (1,1,1)
FEATURE [Part::FeaturePython] Clone005  label="Spacer002"  # Draft clone (typed FeaturePython)
  AttacherType = Attacher::AttachEngine3D
  Fuse = false
  Objects = -> [Body018]
  Placement = pos=(3.81,0,1.5875) rot=(0,1,0;0rad)
  Scale = (1,1,1)
FEATURE [Part::FeaturePython] Clone008  label="ALS-PT204-6C/L178"  # Draft clone (typed FeaturePython)
  AttacherType = Attacher::AttachEngine3D
  Fuse = false
  Objects = -> [Body]
  Placement = pos=(3.81,0,3.6195) rot=(0,0,1;0.785398rad)
  Scale = (1,1,1)
FEATURE [Part::FeaturePython] Clone009  label="VLCS5830-2"  # Draft clone (typed FeaturePython)
  AttacherType = Attacher::AttachEngine3D
  Fuse = false
  Objects = -> [Body001]
  Placement = pos=(3.81,6.35,4.445) rot=(0,0,1;1.5708rad)
  Scale = (1,1,1)
FEATURE [Part::FeaturePython] Clone010  label="VLCS5830-3"  # Draft clone (typed FeaturePython)
  AttacherType = Attacher::AttachEngine3D
  Fuse = false
  Objects = -> [Body001]
  Placement = pos=(3.81,-6.35,4.445) rot=(0,0,1;1.5708rad)
  Scale = (1,1,1)
FEATURE [Part::FeaturePython] Clone011  label="TO-092-1"  # Draft clone (typed FeaturePython)
  AttacherType = Attacher::AttachEngine3D
  Fuse = false
  Objects = -> [Body002]
  Placement = pos=(7.62,-11.43,5.58749) rot=(0,0,1;3.14159rad)
  Scale = (1,1,1)
FEATURE [Part::FeaturePython] Clone012  label="Resistor, 15Ω001"  # Draft clone (typed FeaturePython)
  AttacherType = Attacher::AttachEngine3D
  Fuse = false
  Objects = -> [Body004]
  Placement = pos=(7.62,11.43,3.74693) rot=(0,0,1;0rad)
  Scale = (1,1,1)
FEATURE [Part::FeaturePython] Clone013  label="Resistor, 10KΩ001"  # Draft clone (typed FeaturePython)
  AttacherType = Attacher::AttachEngine3D
  Fuse = false
  Objects = -> [Body009]
  Placement = pos=(12.7,2.54,3.16184) rot=(0,0,1;1.5708rad)
  Scale = (1,1,1)
FEATURE [Part::FeaturePython] Clone015  label="Wire, LED jumper001"  # Draft clone (typed FeaturePython)
  AttacherType = Attacher::AttachEngine3D
  Fuse = false
  Objects = -> [Part003]
  Placement = pos=(3.81,0,1.5875) rot=(0,0,-1;0.321751rad)
  Scale = (1,1,1)
FEATURE [Sketcher::SketchObject] Sketch066
  ExternalGeometry = -> [Sketch033]
  FullyConstrained = true
  MapMode = 5
  Placement = pos=(0,0,0) rot=(0.57735,0.57735,0.57735;2.0944rad)
  Support = -> [YZ_Plane022]
  sketch-geometry (7):
    g0: LineSegment StartX=-3.81 StartY=2.55143 StartZ=0 EndX=-3.81 EndY=0.96393 EndZ=0
    g1: ArcOfCircle CenterX=-2.84607 CenterY=0.96393 CenterZ=0 NormalX=0 NormalY=0 NormalZ=1 AngleXU=0 Radius=0.96393 StartAngle=3.14159 EndAngle=4.71239
    g2: LineSegment StartX=-2.84607 StartY=0 StartZ=0 EndX=2.84607 EndY=0 EndZ=0
    g3: ArcOfCircle CenterX=2.84607 CenterY=0.96393 CenterZ=0 NormalX=0 NormalY=0 NormalZ=1 AngleXU=0 Radius=0.96393 StartAngle=4.71239 EndAngle=6.28319
    g4: LineSegment StartX=3.81 StartY=0.96393 StartZ=0 EndX=3.81 EndY=2.55143 EndZ=0
    g5: LineSegment StartX=-4.13131 StartY=0.96393 StartZ=0 EndX=-3.48869 EndY=0.96393 EndZ=0
    g6: LineSegment StartX=-3.48869 StartY=0.96393 StartZ=0 EndX=-2.84607 EndY=0.96393 EndZ=0
  constraints (18):
    c: Vertical(g0)
    c: Tangent(g0,g1) = -1.5708
    c: Tangent(g1,g2) = -1.5708
    c: Tangent(g2,g3) = -1.5708
    c: Tangent(g3,g4) = -1.5708
    c: Vertical(g4)
    c: Symmetric(g2,g1,g-2)
    c: PointOnObject(g-1,g2)
    c: Coincident(g5,g6)
    c: Equal(g-3,g6)
    c: Equal(g5,g-3)
    c: Symmetric(g5,g5,g0)
    c: Horizontal(g5)
    c: Coincident(g1,g6)
    c: Equal(g1,g3)
    c: Equal(g4,g0)
    c: DistanceY(g0,g0) = 1.5875
    c: DistanceX(g0,g4) = 7.62
FEATURE [PartDesign::AdditivePipe] AdditivePipe012
  AuxilleryCurvelinear = true
  AuxillerySpineTangent = false
  Binormal = (0,0,0)
  Mode = 0
  Placement = pos=(0,0,0) rot=(1,0,0;1.5708rad)
  Profile = -> Sketch033
  Spine = -> Sketch066
  SpineTangent = false
  Transformation = 0
  Transition = 0
FEATURE [PartDesign::Body] Body016
  Group = -> [Sketch033,Sketch066,AdditivePipe012]
  Origin = -> Origin022
  Tip = -> AdditivePipe012
FEATURE [PartDesign::Pad] Pad021
  Direction = (0,-1,-2e-16)
  Length = 5.69214
  Length2 = 10
  Midplane = true
  Placement = pos=(0,0,0) rot=(1,0,0;1.5708rad)
  Profile = -> Sketch038
  ReferenceAxis = -> Sketch038 [N_Axis]
  Type = 0
FEATURE [PartDesign::Body] Body017
  Group = -> [Sketch038,Pad021]
  Origin = -> Origin023
  Tip = -> Pad021
FEATURE [App::Part] Part005  label="Wire, Output"
  Group = -> [Body016,Body017]
  Origin = -> Origin021
  Placement = pos=(-17.78,0,-0.953643) rot=(0,0,1;0rad)
FEATURE [Sketcher::SketchObject] Sketch067
  AttachmentOffset = pos=(0,0,1.27) rot=(0,0,1;0rad)
  ExternalGeometry = -> [Sketch049]
  FullyConstrained = true
  MapMode = 5
  Placement = pos=(0,0,1.27) rot=(0,0,1;0rad)
  Support = -> [XY_Plane026]
  sketch-geometry (2):
    g0: Circle CenterX=0 CenterY=6.35 CenterZ=0 NormalX=0 NormalY=0 NormalZ=1 AngleXU=0 Radius=2.8067
    g1: Circle CenterX=0 CenterY=-6.35 CenterZ=0 NormalX=0 NormalY=0 NormalZ=1 AngleXU=0 Radius=2.8067
  constraints (4):
    c: Coincident(g0,g-3)
    c: Coincident(g1,g-4)
    c: Equal(g1,g0)
    c: Diameter(g0) = 5.6134
FEATURE [PartDesign::Pocket] Pocket009
  BaseFeature = -> Pad016
  Direction = (0,0,-1)
  Length = 5
  Length2 = 5
  Profile = -> Sketch067
  ReferenceAxis = -> Sketch067 [N_Axis]
  Reversed = true
  Type = 1
FEATURE [PartDesign::Body] Body020  label="Shroud"
  Group = -> [Sketch049,Pad016,Sketch067,Pocket009]
  Origin = -> Origin026
  Placement = pos=(-3.81,0,3.175) rot=(0,0,1;0rad)
  Tip = -> Pocket009
FEATURE [TechDraw::DrawProjGroupItem] ProjItem  label="Front"
  CoarseView = false
  Direction = (0,0,1)
  Focus = 100
  HardHidden = false
  IsoCount = 0
  IsoHidden = false
  IsoVisible = false
  LockPosition = true
  Perspective = false
  Rotation = 0
  RotationVector = (1,0,0)
  Scale = 7
  ScaleType = 2
  ScrubCount = 0
  SeamHidden = false
  SeamVisible = true
  SmoothHidden = false
  SmoothVisible = true
  Source = -> [Body018]
  Type = 0
  X = 0
  XDirection = (1,0,0)
  Y = 0
FEATURE [TechDraw::DrawProjGroupItem] ProjItem007  label="Left"
  CoarseView = false
  Direction = (-1,0,1e-16)
  Focus = 100
  HardHidden = false
  IsoCount = 0
  IsoHidden = false
  IsoVisible = false
  LockPosition = false
  Perspective = false
  Rotation = 0
  RotationVector = (1,0,0)
  Scale = 7
  ScaleType = 2
  ScrubCount = 0
  SeamHidden = false
  SeamVisible = true
  SmoothHidden = false
  SmoothVisible = true
  Source = -> [Body018]
  Type = 1
  X = -54.61
  XDirection = (1e-16,0,1)
  Y = 0
FEATURE [TechDraw::DrawProjGroup] ProjGroup
  Anchor = -> ProjItem
  AutoDistribute = false
  LockPosition = false
  ProjectionType = 1
  Rotation = 0
  Scale = 7
  ScaleType = 0
  Source = -> [Body018]
  Views = -> [ProjItem,ProjItem007]
  X = 83.82
  Y = 100
  spacingX = 15
  spacingY = 15
FEATURE [TechDraw::DrawViewDimension] Dimension
  AngleOverride = false
  Arbitrary = true
  ArbitraryTolerances = false
  EqualTolerance = true
  ExtensionAngle = 0
  FormatSpec = 1/16
  FormatSpecOverTolerance = %+.3w
  FormatSpecUnderTolerance = %+.3w
  Inverted = false
  LineAngle = 0
  LockPosition = false
  MeasureType = 1
  OverTolerance = 0
  References2D = -> [ProjItem007]
  Rotation = 0
  Scale = 7
  ScaleType = 0
  TheoreticalExact = false
  Type = 1
  UnderTolerance = 0
  X = 19.7881
  Y = -69.6723
FEATURE [TechDraw::DrawViewDimension] Dimension043
  AngleOverride = false
  Arbitrary = false
  ArbitraryTolerances = false
  EqualTolerance = true
  ExtensionAngle = 0
  FormatSpec = %.3w
  FormatSpecOverTolerance = %+.3w
  FormatSpecUnderTolerance = %+.3w
  Inverted = false
  LineAngle = 0
  LockPosition = false
  MeasureType = 1
  OverTolerance = 0
  References2D = -> [ProjItem007]
  Rotation = 0
  Scale = 7
  ScaleType = 0
  TheoreticalExact = false
  Type = 2
  UnderTolerance = 0
  X = -13.7353
  Y = 0.351747
FEATURE [TechDraw::DrawViewDimension] Dimension044
  AngleOverride = false
  Arbitrary = false
  ArbitraryTolerances = false
  EqualTolerance = true
  ExtensionAngle = 0
  FormatSpec = %.3w
  FormatSpecOverTolerance = %+.3w
  FormatSpecUnderTolerance = %+.3w
  Inverted = false
  LineAngle = 0
  LockPosition = false
  MeasureType = 1
  OverTolerance = 0
  References2D = -> [ProjItem]
  Rotation = 0
  Scale = 7
  ScaleType = 0
  TheoreticalExact = false
  Type = 1
  UnderTolerance = 0
  X = -0.795337
  Y = 85.5277
FEATURE [TechDraw::DrawViewDimension] Dimension045
  AngleOverride = false
  Arbitrary = false
  ArbitraryTolerances = false
  EqualTolerance = true
  ExtensionAngle = 0
  FormatSpec = %.3w
  FormatSpecOverTolerance = %+.3w
  FormatSpecUnderTolerance = %+.3w
  Inverted = false
  LineAngle = 0
  LockPosition = false
  MeasureType = 1
  OverTolerance = 0
  References2D = -> [ProjItem]
  Rotation = 0
  Scale = 7
  ScaleType = 0
  TheoreticalExact = false
  Type = 1
  UnderTolerance = 0
  X = 39.4813
  Y = 78.9631
FEATURE [TechDraw::DrawViewDimension] Dimension046
  AngleOverride = false
  Arbitrary = false
  ArbitraryTolerances = false
  EqualTolerance = true
  ExtensionAngle = 0
  FormatSpec = %.3w
  FormatSpecOverTolerance = %+.3w
  FormatSpecUnderTolerance = %+.3w
  Inverted = false
  LineAngle = 0
  LockPosition = false
  MeasureType = 1
  OverTolerance = 0
  References2D = -> [ProjItem]
  Rotation = 0
  Scale = 7
  ScaleType = 0
  TheoreticalExact = false
  Type = 1
  UnderTolerance = 0
  X = 38.979
  Y = 73.2822
FEATURE [TechDraw::DrawViewDimension] Dimension047
  AngleOverride = false
  Arbitrary = false
  ArbitraryTolerances = false
  EqualTolerance = true
  ExtensionAngle = 0
  FormatSpec = %.3w
  FormatSpecOverTolerance = %+.3w
  FormatSpecUnderTolerance = %+.3w
  Inverted = false
  LineAngle = 0
  LockPosition = false
  MeasureType = 1
  OverTolerance = 0
  References2D = -> [ProjItem]
  Rotation = 0
  Scale = 7
  ScaleType = 0
  TheoreticalExact = false
  Type = 1
  UnderTolerance = 0
  X = 39.2503
  Y = -74.9851
FEATURE [TechDraw::DrawViewDimension] Dimension048
  AngleOverride = false
  Arbitrary = false
  ArbitraryTolerances = false
  EqualTolerance = true
  ExtensionAngle = 0
  FormatSpec = %.3w
  FormatSpecOverTolerance = %+.3w
  FormatSpecUnderTolerance = %+.3w
  Inverted = false
  LineAngle = 0
  LockPosition = false
  MeasureType = 1
  OverTolerance = 0
  References2D = -> [ProjItem]
  Rotation = 0
  Scale = 7
  ScaleType = 0
  TheoreticalExact = false
  Type = 1
  UnderTolerance = 0
  X = 38.3074
  Y = -69.2702
FEATURE [TechDraw::DrawViewDimension] Dimension049
  AngleOverride = false
  Arbitrary = false
  ArbitraryTolerances = false
  EqualTolerance = true
  ExtensionAngle = 0
  FormatSpec = %.3w
  FormatSpecOverTolerance = %+.3w
  FormatSpecUnderTolerance = %+.3w
  Inverted = false
  LineAngle = 0
  LockPosition = false
  MeasureType = 1
  OverTolerance = 0
  References2D = -> [ProjItem]
  Rotation = 0
  Scale = 7
  ScaleType = 0
  TheoreticalExact = false
  Type = 2
  UnderTolerance = 0
  X = 29.8736
  Y = 35.3491
FEATURE [TechDraw::DrawViewDimension] Dimension050
  AngleOverride = false
  Arbitrary = false
  ArbitraryTolerances = false
  EqualTolerance = true
  ExtensionAngle = 0
  FormatSpec = %.3w
  FormatSpecOverTolerance = %+.3w
  FormatSpecUnderTolerance = %+.3w
  Inverted = false
  LineAngle = 0
  LockPosition = false
  MeasureType = 1
  OverTolerance = 0
  References2D = -> [ProjItem]
  Rotation = 0
  Scale = 7
  ScaleType = 0
  TheoreticalExact = false
  Type = 2
  UnderTolerance = 0
  X = 38.3413
  Y = 15.0955
FEATURE [TechDraw::DrawViewDimension] Dimension051
  AngleOverride = false
  Arbitrary = false
  ArbitraryTolerances = false
  EqualTolerance = true
  ExtensionAngle = 0
  FormatSpec = %.3w
  FormatSpecOverTolerance = %+.3w
  FormatSpecUnderTolerance = %+.3w
  Inverted = false
  LineAngle = 0
  LockPosition = false
  MeasureType = 1
  OverTolerance = 0
  References2D = -> [ProjItem]
  Rotation = 0
  Scale = 7
  ScaleType = 0
  TheoreticalExact = false
  Type = 2
  UnderTolerance = 0
  X = -30.388
  Y = 37.2852
FEATURE [TechDraw::DrawViewDimension] Dimension052
  AngleOverride = false
  Arbitrary = false
  ArbitraryTolerances = false
  EqualTolerance = true
  ExtensionAngle = 0
  FormatSpec = %.3w
  FormatSpecOverTolerance = %+.3w
  FormatSpecUnderTolerance = %+.3w
  Inverted = false
  LineAngle = 0
  LockPosition = false
  MeasureType = 1
  OverTolerance = 0
  References2D = -> [ProjItem]
  Rotation = 0
  Scale = 7
  ScaleType = 0
  TheoreticalExact = false
  Type = 2
  UnderTolerance = 0
  X = 47.2573
  Y = -15.8044
FEATURE [TechDraw::DrawViewDimension] Dimension053
  AngleOverride = false
  Arbitrary = true
  ArbitraryTolerances = false
  EqualTolerance = true
  ExtensionAngle = 0
  FormatSpec = 1/16
  FormatSpecOverTolerance = %+.3w
  FormatSpecUnderTolerance = %+.3w
  Inverted = false
  LineAngle = 0
  LockPosition = false
  MeasureType = 1
  OverTolerance = 0
  References2D = -> [ProjItem]
  Rotation = 0
  Scale = 7
  ScaleType = 0
  TheoreticalExact = false
  Type = 5
  UnderTolerance = 0
  X = -31.9271
  Y = -5.11288
FEATURE [TechDraw::DrawPage] Page  label="Spacer drawing"
  KeepUpdated = true
  NextBalloonIndex = 1
  ProjectionType = 1
  Scale = 7
  Template = -> Template
  Views = -> [ProjGroup,Dimension,Dimension043,Dimension044,Dimension045,Dimension046,Dimension047,Dimension048,Dimension049,Dimension050,Dimension051,Dimension052,Dimension053]
FEATURE [TechDraw::DrawProjGroupItem] ProjItem008  label="Front005"
  CoarseView = false
  Direction = (0,0,1)
  Focus = 100
  HardHidden = false
  IsoCount = 0
  IsoHidden = false
  IsoVisible = false
  LockPosition = true
  Perspective = false
  Rotation = 0
  RotationVector = (1,0,0)
  Scale = 5
  ScaleType = 2
  ScrubCount = 0
  SeamHidden = false
  SeamVisible = true
  SmoothHidden = false
  SmoothVisible = true
  Source = -> [Body020]
  Type = 0
  X = 0
  XDirection = (1,0,0)
  Y = 0
FEATURE [TechDraw::DrawProjGroup] ProjGroup005
  Anchor = -> ProjItem008
  AutoDistribute = true
  LockPosition = false
  ProjectionType = 1
  Rotation = 0
  Scale = 5
  ScaleType = 0
  Source = -> [Body020]
  Views = -> [ProjItem008]
  X = 35.56
  Y = 100
  spacingX = 15
  spacingY = 15
FEATURE [TechDraw::DrawViewSection] SectionView004  label="Section A - A004"
  BaseView = -> ProjItem008
  Caption = Section A - A
  CoarseView = false
  CutSurfaceDisplay = 3
  Direction = (1,0,0)
  FileGeomPattern = /Applications/FreeCAD.app/Contents/Resources/share/Mod/TechDraw/PAT/FCPAT.pat
  FileHatchPattern = /Applications/FreeCAD.app/Contents/Resources/share/Mod/TechDraw/Patterns/simple.svg
  Focus = 100
  FuseBeforeCut = false
  HardHidden = false
  HatchOffset = (0,0,0)
  HatchRotation = 0
  HatchScale = 1
  IsoCount = 0
  IsoHidden = false
  IsoVisible = false
  LockPosition = false
  NameGeomPattern = Diagonal4
  Perspective = false
  Rotation = 90
  Scale = 5
  ScaleType = 0
  ScrubCount = 0
  SeamHidden = false
  SeamVisible = true
  SectionDirection = 4
  SectionNormal = (1,0,0)
  SectionOrigin = (-3.81,0,8.255)
  SectionSymbol = A
  SmoothHidden = false
  SmoothVisible = true
  Source = -> [Body020]
  TrimAfterCut = false
  X = 107.95
  XDirection = (0,1,0)
  Y = 100
FEATURE [TechDraw::DrawViewDimension] Dimension054
  AngleOverride = false
  Arbitrary = false
  ArbitraryTolerances = false
  EqualTolerance = true
  ExtensionAngle = 0
  FormatSpec = %.3w
  FormatSpecOverTolerance = %+.3w
  FormatSpecUnderTolerance = %+.3w
  Inverted = false
  LineAngle = 0
  LockPosition = false
  MeasureType = 1
  OverTolerance = 0
  References2D = -> [SectionView004]
  Rotation = 0
  Scale = 5
  ScaleType = 0
  TheoreticalExact = false
  Type = 2
  UnderTolerance = 0
  X = 32.3966
  Y = 1.70901
FEATURE [TechDraw::DrawViewDimension] Dimension055
  AngleOverride = false
  Arbitrary = false
  ArbitraryTolerances = false
  EqualTolerance = true
  ExtensionAngle = 0
  FormatSpec = %.3w
  FormatSpecOverTolerance = %+.3w
  FormatSpecUnderTolerance = %+.3w
  Inverted = false
  LineAngle = 0
  LockPosition = false
  MeasureType = 1
  OverTolerance = 0
  References2D = -> [SectionView004]
  Rotation = 0
  Scale = 5
  ScaleType = 0
  TheoreticalExact = false
  Type = 1
  UnderTolerance = 0
  X = 1.5572
  Y = 65.8065
FEATURE [TechDraw::DrawViewDimension] Dimension056
  AngleOverride = false
  Arbitrary = false
  ArbitraryTolerances = false
  EqualTolerance = true
  ExtensionAngle = 0
  FormatSpec = %.3w
  FormatSpecOverTolerance = %+.3w
  FormatSpecUnderTolerance = %+.3w
  Inverted = false
  LineAngle = 0
  LockPosition = false
  MeasureType = 1
  OverTolerance = 0
  References2D = -> [SectionView004]
  Rotation = 0
  Scale = 5
  ScaleType = 0
  TheoreticalExact = false
  Type = 1
  UnderTolerance = 0
  X = -2.49237
  Y = -56.7049
FEATURE [TechDraw::DrawViewDimension] Dimension057
  AngleOverride = false
  Arbitrary = false
  ArbitraryTolerances = false
  EqualTolerance = true
  ExtensionAngle = 0
  FormatSpec = %.3w
  FormatSpecOverTolerance = %+.3w
  FormatSpecUnderTolerance = %+.3w
  Inverted = false
  LineAngle = 0
  LockPosition = false
  MeasureType = 1
  OverTolerance = 0
  References2D = -> [ProjItem008]
  Rotation = 0
  Scale = 5
  ScaleType = 0
  TheoreticalExact = false
  Type = 1
  UnderTolerance = 0
  X = -0.479139
  Y = 64.0098
FEATURE [TechDraw::DrawViewDimension] Dimension058
  AngleOverride = false
  Arbitrary = false
  ArbitraryTolerances = false
  EqualTolerance = true
  ExtensionAngle = 0
  FormatSpec = %.3w
  FormatSpecOverTolerance = %+.3w
  FormatSpecUnderTolerance = %+.3w
  Inverted = false
  LineAngle = 0
  LockPosition = false
  MeasureType = 1
  OverTolerance = 0
  References2D = -> [ProjItem008]
  Rotation = 0
  Scale = 5
  ScaleType = 0
  TheoreticalExact = false
  Type = 2
  UnderTolerance = 0
  X = -24.2282
  Y = 23.1258
FEATURE [TechDraw::DrawViewDimension] Dimension059
  AngleOverride = false
  Arbitrary = false
  ArbitraryTolerances = false
  EqualTolerance = true
  ExtensionAngle = 0
  FormatSpec = %.3w
  FormatSpecOverTolerance = %+.3w
  FormatSpecUnderTolerance = %+.3w
  Inverted = false
  LineAngle = 0
  LockPosition = false
  MeasureType = 1
  OverTolerance = 0
  References2D = -> [ProjItem008]
  Rotation = 0
  Scale = 5
  ScaleType = 0
  TheoreticalExact = false
  Type = 2
  UnderTolerance = 0
  X = 23.3897
  Y = 19.1166
FEATURE [TechDraw::DrawViewDimension] Dimension060
  AngleOverride = false
  Arbitrary = false
  ArbitraryTolerances = false
  EqualTolerance = true
  ExtensionAngle = 0
  FormatSpec = %.3w
  FormatSpecOverTolerance = %+.3w
  FormatSpecUnderTolerance = %+.3w
  Inverted = false
  LineAngle = 0
  LockPosition = false
  MeasureType = 1
  OverTolerance = 0
  References2D = -> [ProjItem008]
  Rotation = 0
  Scale = 5
  ScaleType = 0
  TheoreticalExact = false
  Type = 2
  UnderTolerance = 0
  X = 31.6549
  Y = -10.4773
FEATURE [TechDraw::DrawViewDimension] Dimension061
  AngleOverride = false
  Arbitrary = false
  ArbitraryTolerances = false
  EqualTolerance = true
  ExtensionAngle = 0
  FormatSpec = Ø%.3w(#2)
  FormatSpecOverTolerance = %+.3w
  FormatSpecUnderTolerance = %+.3w
  Inverted = false
  LineAngle = 0
  LockPosition = false
  MeasureType = 1
  OverTolerance = 0
  References2D = -> [ProjItem008]
  Rotation = 0
  Scale = 5
  ScaleType = 0
  TheoreticalExact = false
  Type = 5
  UnderTolerance = 0
  X = 1.31763
  Y = -68.996
FEATURE [TechDraw::DrawViewDimension] Dimension062
  AngleOverride = false
  Arbitrary = false
  ArbitraryTolerances = false
  EqualTolerance = true
  ExtensionAngle = 0
  FormatSpec = Ø%.3w(#19)
  FormatSpecOverTolerance = %+.3w
  FormatSpecUnderTolerance = %+.3w
  Inverted = false
  LineAngle = 0
  LockPosition = false
  MeasureType = 1
  OverTolerance = 0
  References2D = -> [ProjItem008]
  Rotation = 0
  Scale = 5
  ScaleType = 0
  TheoreticalExact = false
  Type = 5
  UnderTolerance = 0
  X = 11.9785
  Y = -61.3298
FEATURE [TechDraw::DrawPage] Page002  label="Shroud drawing"
  KeepUpdated = true
  NextBalloonIndex = 1
  ProjectionType = 1
  Scale = 5
  Template = -> Template002
  Views = -> [ProjGroup005,SectionView004,Dimension054,Dimension055,Dimension056,Dimension057,Dimension058,Dimension059,Dimension060,Dimension061,Dimension062]
FEATURE [Part::FeaturePython] Clone016  label="Wire, Return001"  # Draft clone (typed FeaturePython)
  AttacherType = Attacher::AttachEngine3D
  Fuse = false
  Objects = -> [Part]
  Placement = pos=(10.16,0,0) rot=(0,0,1;0rad)
  Scale = (1,1,1)
FEATURE [Part::FeaturePython] Clone017  label="Shroud001"  # Draft clone (typed FeaturePython)
  AttacherType = Attacher::AttachEngine3D
  Fuse = false
  Objects = -> [Body020]
  Placement = pos=(3.81,0,3.175) rot=(0,0,1;0rad)
  Scale = (1,1,1)
FEATURE [Part::FeaturePython] Clone019  label="Wire, Detect001"  # Draft clone (typed FeaturePython)
  AttacherType = Attacher::AttachEngine3D
  Fuse = false
  Objects = -> [Part002]
  Placement = pos=(17.78,1.27,0) rot=(0,0,1;0rad)
  Scale = (1,1,1)
FEATURE [Sketcher::SketchObject] Sketch068
  FullyConstrained = true
  MapMode = 5
  Support = -> [XY_Plane034]
  sketch-geometry (1):
    g0: Circle CenterX=0 CenterY=0 CenterZ=0 NormalX=0 NormalY=0 NormalZ=1 AngleXU=0 Radius=0.32131
  constraints (2):
    c: Coincident(g0,g-1)
    c: Diameter(g0) = 0.64262
FEATURE [Sketcher::SketchObject] Sketch069
  ExternalGeometry = -> [Sketch068]
  FullyConstrained = true
  MapMode = 5
  Placement = pos=(0,0,0) rot=(0.57735,0.57735,0.57735;2.0944rad)
  Support = -> [YZ_Plane034]
  sketch-geometry (9):
    g0: LineSegment StartX=-8.4618e-12 StartY=0 StartZ=0 EndX=-8.4618e-12 EndY=1.5875 EndZ=0
    g1: ArcOfCircle CenterX=-0.96393 CenterY=1.5875 CenterZ=0 NormalX=0 NormalY=0 NormalZ=1 AngleXU=0 Radius=0.96393 StartAngle=3.80798e-11 EndAngle=1.5708
    g2: LineSegment StartX=-0.96393 StartY=2.55143 StartZ=0 EndX=-4.68073 EndY=2.55143 EndZ=0
    g3: ArcOfCircle CenterX=-4.68073 CenterY=3.51536 CenterZ=0 NormalX=0 NormalY=0 NormalZ=1 AngleXU=0 Radius=0.96393 StartAngle=3.92699 EndAngle=4.71239
    g4: LineSegment StartX=-5.36233 StartY=2.83376 StartZ=0 EndX=-6.00495 EndY=3.47638 EndZ=0
    g5: LineSegment StartX=-6.00495 StartY=3.47638 StartZ=0 EndX=-5.36233 EndY=3.47638 EndZ=0
    g6: LineSegment StartX=-5.36233 StartY=3.47638 StartZ=0 EndX=-5.36233 EndY=2.83376 EndZ=0
    g7: GeomPoint X=-5.08 Y=2.55143 Z=0
    g8: LineSegment StartX=-0.96393 StartY=1.5875 StartZ=0 EndX=-0.32131 EndY=1.5875 EndZ=0
  constraints (23):
    c: Coincident(g-1,g0)
    c: Vertical(g0)
    c: Tangent(g0,g1) = -1.5708
    c: Tangent(g1,g2) = -1.5708
    c: Horizontal(g2)
    c: Tangent(g2,g3) = 1.5708
    c: Tangent(g3,g4) = 1.5708
    c: Coincident(g4,g5)
    c: Horizontal(g5)
    c: Coincident(g5,g6)
    c: Coincident(g6,g3)
    c: Vertical(g6)
    c: Equal(g6,g-3)
    c: Equal(g5,g-3)
    c: Equal(g1,g3)
    c: PointOnObject(g7,g4)
    c: PointOnObject(g7,g2)
    c: DistanceX(g7,g-1) = 5.08
    c: Coincident(g8,g1)
    c: Horizontal(g8)
    c: Equal(g8,g-3)
    c: Vertical(g8,g-3)
    c: DistanceY(g0,g0) = 1.5875
FEATURE [Sketcher::SketchObject] Sketch070
  ExternalGeometry = -> [Sketch069]
  FullyConstrained = true
  MapMode = 1
  Placement = pos=(-1.6e-15,-4.68073,2.55143) rot=(0,0,1;0rad)
  Support = -> [Sketch069]
  sketch-geometry (7):
    g0: ArcOfCircle CenterX=-0.96393 CenterY=3e-16 CenterZ=0 NormalX=0 NormalY=0 NormalZ=1 AngleXU=0 Radius=0.96393 StartAngle=5.49779 EndAngle=6.28319
    g1: LineSegment StartX=-0.282329 StartY=-0.681601 StartZ=0 EndX=-6.9384 EndY=-7.33767 EndZ=0
    g2: LineSegment StartX=-0.96393 StartY=3e-16 StartZ=0 EndX=-0.282329 EndY=-0.681601 EndZ=0
    g3: LineSegment StartX=-0.282329 StartY=-0.681601 StartZ=0 EndX=-0.282329 EndY=-7.33767 EndZ=0
    g4: LineSegment StartX=-0.282329 StartY=-7.33767 StartZ=0 EndX=-6.9384 EndY=-7.33767 EndZ=0
    g5: ArcOfCircle CenterX=-7.62 CenterY=-6.65607 CenterZ=0 NormalX=0 NormalY=0 NormalZ=1 AngleXU=0 Radius=0.96393 StartAngle=3.92699 EndAngle=5.49779
    g6: LineSegment StartX=-7.62 StartY=-8.01927 StartZ=0 EndX=-8.3016 EndY=-7.33767 EndZ=0
  constraints (17):
    c: Tangent(g-3,g0) = 1.5708
    c: Tangent(g0,g1) = 1.5708
    c: Coincident(g2,g0)
    c: Coincident(g2,g0)
    c: Coincident(g3,g0)
    c: Vertical(g3)
    c: Coincident(g4,g3)
    c: Coincident(g4,g1)
    c: Horizontal(g4)
    c: Equal(g4,g3)
    c: Equal(g2,g-4)
    c: Tangent(g5,g1) = 1.5708
    c: Tangent(g6,g5) = 1.5708
    c: Perpendicular(g1,g6)
    c: PointOnObject(g6,g1)
    c: Equal(g6,g-4)
    c: DistanceX(g6,g-1) = 7.62
FEATURE [Sketcher::SketchObject] Sketch071
  ExternalGeometry = -> [Sketch070]
  FullyConstrained = true
  MapMode = 1
  Placement = pos=(-6.9384,-12.0184,2.55143) rot=(0,0,1;0rad)
  Support = -> [Sketch070]
  sketch-geometry (1):
    g0: LineSegment StartX=0 StartY=0 StartZ=0 EndX=6.65607 EndY=-6.65607 EndZ=0
  constraints (3):
    c: Coincident(g0,g-1)
    c: Perpendicular(g0,g-3)
    c: Equal(g0,g-3)
FEATURE [Sketcher::SketchObject] Sketch072
  ExternalGeometry = -> [Sketch068]
  FullyConstrained = true
  MapMode = 47
  Placement = pos=(-6.9384,-12.0184,2.55143) rot=(0.862856,0.357407,0.357407;1.71777rad)
  Support = -> [Sketch071,Sketch070]
  sketch-geometry (4):
    g0: ArcOfCircle CenterX=0 CenterY=-0.96393 CenterZ=0 NormalX=0 NormalY=0 NormalZ=1 AngleXU=0 Radius=0.96393 StartAngle=1.5708 EndAngle=3.14159
    g1: LineSegment StartX=-0.96393 StartY=-0.96393 StartZ=0 EndX=-0.96393 EndY=-2.55143 EndZ=0
    g2: LineSegment StartX=0 StartY=-0.96393 StartZ=0 EndX=-0.64262 EndY=-0.96393 EndZ=0
    g3: LineSegment StartX=-0.64262 StartY=-0.96393 StartZ=0 EndX=-1.28524 EndY=-0.96393 EndZ=0
  constraints (12):
    c: PointOnObject(g0,g-2)
    c: PointOnObject(g0,g-2)
    c: Tangent(g0,g-1)
    c: Tangent(g0,g1) = -1.5708
    c: Coincident(g2,g0)
    c: Horizontal(g2)
    c: Coincident(g2,g3)
    c: Horizontal(g3)
    c: Equal(g2,g-3)
    c: Equal(g-3,g3)
    c: Symmetric(g3,g2,g0)
    c: PointOnObject(g1,g-3)
FEATURE [Sketcher::SketchObject] Sketch073
  FullyConstrained = true
  MapMode = 5
  Support = -> [XY_Plane036]
  sketch-geometry (11):
    g0: Circle CenterX=0 CenterY=0 CenterZ=0 NormalX=0 NormalY=0 NormalZ=1 AngleXU=0 Radius=0.32131
    g1: LineSegment StartX=0 StartY=0.32131 StartZ=0 EndX=0 EndY=-0.32131 EndZ=0
    g2: LineSegment StartX=0 StartY=-0.32131 StartZ=0 EndX=0 EndY=-0.96393 EndZ=0
    g3: LineSegment StartX=0 StartY=-0.96393 StartZ=0 EndX=0 EndY=-4.68073 EndZ=0
    g4: ArcOfCircle CenterX=-0.96393 CenterY=-4.68073 CenterZ=0 NormalX=0 NormalY=0 NormalZ=1 AngleXU=0 Radius=0.96393 StartAngle=5.49779 EndAngle=6.28319
    g5: LineSegment StartX=-0.282329 StartY=-5.36233 StartZ=0 EndX=-6.9384 EndY=-12.0184 EndZ=0
    g6: LineSegment StartX=-6.9384 StartY=-12.0184 StartZ=0 EndX=-0.282329 EndY=-12.0184 EndZ=0
    g7: LineSegment StartX=-0.282329 StartY=-12.0184 StartZ=0 EndX=-0.282329 EndY=-5.36233 EndZ=0
    g8: GeomPoint X=0 Y=-5.08 Z=0
    g9: Circle CenterX=0 CenterY=0 CenterZ=0 NormalX=0 NormalY=0 NormalZ=1 AngleXU=0 Radius=0.96393
    g10: Circle CenterX=-7.62 CenterY=-12.7 CenterZ=0 NormalX=0 NormalY=0 NormalZ=1 AngleXU=0 Radius=0.96393
  constraints (29):
    c: Coincident(g0,g-1)
    c: Diameter(g0) = 0.64262
    c: Vertical(g1)
    c: Coincident(g1,g2)
    c: Vertical(g2)
    c: Equal(g2,g1)
    c: PointOnObject(g1,g-2)
    c: PointOnObject(g1,g0)
    c: PointOnObject(g1,g0)
    c: Coincident(g2,g3)
    c: Vertical(g3)
    c: Tangent(g3,g4) = 1.5708
    c: Tangent(g4,g5) = 1.5708
    c: Coincident(g5,g6)
    c: Horizontal(g6)
    c: Coincident(g6,g7)
    c: Coincident(g7,g4)
    c: Vertical(g7)
    c: Equal(g7,g6)
    c: PointOnObject(g8,g-2)
    c: PointOnObject(g8,g5)
    c: DistanceY(g8,g-1) = 5.08
    c: Coincident(g9,g0)
    c: PointOnObject(g3,g9)
    c: Equal(g9,g4)
    c: PointOnObject(g5,g10)
    c: PointOnObject(g10,g5)
    c: Equal(g10,g9)
    c: DistanceX(g10,g-1) = 7.62
FEATURE [Sketcher::SketchObject] Sketch074
  FullyConstrained = true
  MapMode = 1
  Placement = pos=(0,-0.96393,0) rot=(1,0,0;1.5708rad)
  Support = -> [Sketch073]
  sketch-geometry (1):
    g0: Circle CenterX=0 CenterY=0 CenterZ=0 NormalX=0 NormalY=0 NormalZ=1 AngleXU=0 Radius=0.762
  constraints (2):
    c: Coincident(g0,g-1)
    c: Diameter(g0) = 1.524
FEATURE [PartDesign::AdditivePipe] AdditivePipe014
  AuxilleryCurvelinear = true
  AuxillerySpineTangent = false
  Binormal = (0,0,0)
  Mode = 0
  Profile = -> Sketch074
  Spine = -> Sketch073
  SpineTangent = false
  Transformation = 0
  Transition = 0
FEATURE [PartDesign::Body] Body028
  Group = -> [Sketch073,Sketch074,AdditivePipe014]
  Origin = -> Origin036
  Placement = pos=(0,0,2.55143) rot=(0,0,1;0rad)
  Tip = -> AdditivePipe014
FEATURE [PartDesign::SubShapeBinder] Binder
  BindCopyOnChange = 0
  BindMode = 0
  ClaimChildren = false
  Context = -> Part007 [Body027.Binder.]
  Fuse = false
  MakeFace = true
  OffsetFill = false
  OffsetIntersection = false
  OffsetJoinType = 0
  OffsetOpenResult = false
  PartialLoad = false
  Relative = true
  Support = -> [Sketch069,Sketch070,Sketch072]
  _Version = 2
FEATURE [PartDesign::AdditivePipe] AdditivePipe015
  AuxilleryCurvelinear = true
  AuxillerySpineTangent = false
  Binormal = (0,0,0)
  Mode = 0
  Profile = -> Sketch068
  Spine = -> Binder
  SpineTangent = false
  Transformation = 0
  Transition = 0
FEATURE [PartDesign::Body] Body027
  Group = -> [Sketch068,Sketch069,Sketch070,Sketch071,Sketch072,Binder,AdditivePipe015]
  Origin = -> Origin034
  Tip = -> AdditivePipe015
FEATURE [App::Part] Part007  label="Wire, Switch001"
  Group = -> [Body027,Body028]
  Origin = -> Origin035
  Placement = pos=(15.24,3.81,0) rot=(0,0,1;0rad)
FEATURE [Part::Feature] Part__Feature001  label="Screw, Sheet Metal, Pan Head, Phillips, #8x1p25"
  Placement = pos=(-22.86,0,1.5875) rot=(0,0,1;0rad)
  shape: bbox 7.423 x 7.423 x 34.21 mm, 87 faces (baked)
